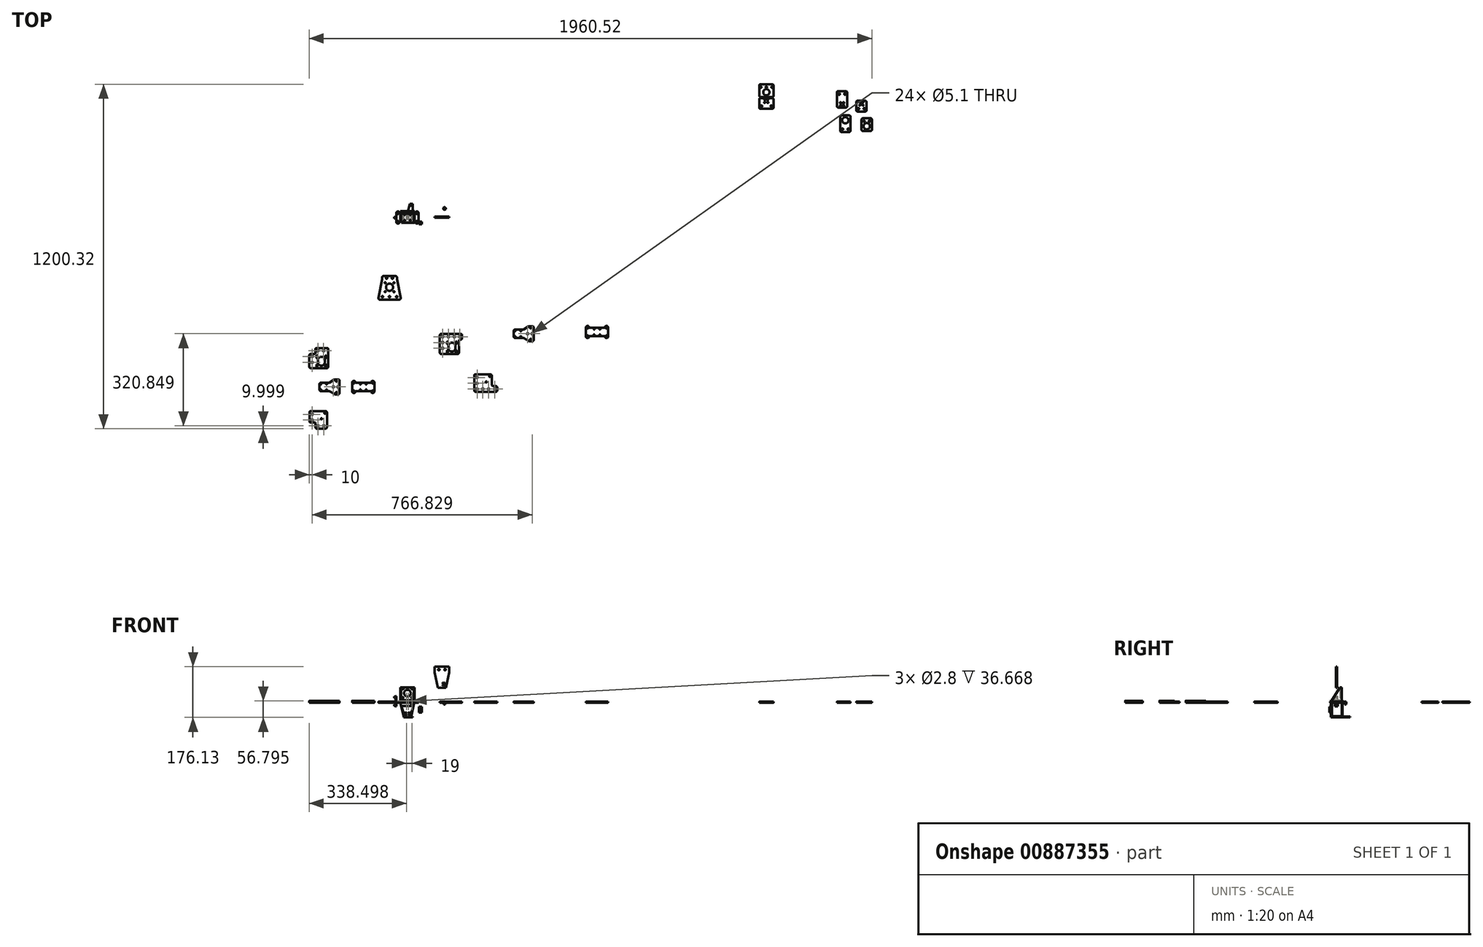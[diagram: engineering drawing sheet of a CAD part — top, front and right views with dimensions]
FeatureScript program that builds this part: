
annotation { "Feature Type Name" : "Feature", "Feature Type Description" : "" }
export const myFeature = defineFeature(function(context is Context, id is Id, definition is map)
    precondition{}
    {
        {
            var Q0;
            Q0=qCreatedBy(makeId("Top.planeOp"),FACE);
            var sketch = newSketch(context, id + "F0", { "sketchPlane" : qUnion([Q0])});
            skCircle(sketch, "E0", {"center": v(-667.66, -487.54) * mm, "radius": 2.55 * mm});
            skCircle(sketch, "E1", {"center": v(-667.66, -507.54) * mm, "radius": 2.55 * mm});
            skLineSegment(sketch, "E2.top", {"start": v(-677.66, -483.54) * mm, "end": v(-677.66, -522.54) * mm});
            skLineSegment(sketch, "E2.left", {"start": v(-620.16, -457.54) * mm, "end": v(-651.66, -457.54) * mm});
            skLineSegment(sketch, "E2.right", {"start": v(-620.16, -527.54) * mm, "end": v(-672.66, -527.54) * mm});
            skLineSegment(sketch, "E3.top", {"start": v(-656.66, -462.54) * mm, "end": v(-656.66, -478.54) * mm});
            skLineSegment(sketch, "E3.right", {"start": v(-672.66, -478.54) * mm, "end": v(-656.66, -478.54) * mm});
            skLineSegment(sketch, "E4", {"start": v(-620.16, -491.36) * mm, "end": v(-620.16, -485.36) * mm});
            skLineSegment(sketch, "E5", {"start": v(-651.16, -491.36) * mm, "end": v(-651.16, -485.36) * mm});
            skLineSegment(sketch, "E6", {"start": v(-620.16, -522.36) * mm, "end": v(-620.16, -516.36) * mm});
            skLineSegment(sketch, "E7", {"start": v(-623.41, -500.36) * mm, "end": v(-623.41, -506.86) * mm});
            skLineSegment(sketch, "E8", {"start": v(-647.91, -500.36) * mm, "end": v(-647.91, -506.86) * mm});
            skArc(sketch, "E9", {"start": v(-623.41, -500.36) * mm, "mid": v(-635.66, -488.1) * mm, "end": v(-647.91, -500.36) * mm});
            skArc(sketch, "E10", {"start": v(-647.91, -506.86) * mm, "mid": v(-635.66, -519.1) * mm, "end": v(-623.41, -506.86) * mm});
            skLineSegment(sketch, "E11", {"start": v(-621.75, -516.3) * mm, "end": v(-621.75, -522.32) * mm});
            skLineSegment(sketch, "E12", {"start": v(-618.57, -516.3) * mm, "end": v(-618.57, -522.32) * mm});
            skLineSegment(sketch, "E13", {"start": v(-649.58, -516.27) * mm, "end": v(-649.57, -522.32) * mm});
            skLineSegment(sketch, "E14", {"start": v(-652.75, -516.3) * mm, "end": v(-652.75, -522.35) * mm});
            skLineSegment(sketch, "E15", {"start": v(-651.16, -516.36) * mm, "end": v(-651.16, -522.36) * mm});
            skLineSegment(sketch, "E16", {"start": v(-652.75, -485.36) * mm, "end": v(-652.75, -491.37) * mm});
            skLineSegment(sketch, "E17", {"start": v(-649.57, -485.36) * mm, "end": v(-649.57, -491.37) * mm});
            skLineSegment(sketch, "E18", {"start": v(-621.75, -485.35) * mm, "end": v(-621.75, -491.35) * mm});
            skLineSegment(sketch, "E19", {"start": v(-618.57, -485.35) * mm, "end": v(-618.57, -491.35) * mm});
            skArc(sketch, "E20", {"start": v(-618.57, -485.35) * mm, "mid": v(-620.16, -483.76) * mm, "end": v(-621.75, -485.35) * mm});
            skArc(sketch, "E21", {"start": v(-621.75, -491.35) * mm, "mid": v(-620.16, -492.94) * mm, "end": v(-618.57, -491.35) * mm});
            skArc(sketch, "E22", {"start": v(-649.57, -485.36) * mm, "mid": v(-651.16, -483.77) * mm, "end": v(-652.75, -485.36) * mm});
            skArc(sketch, "E23", {"start": v(-652.75, -491.37) * mm, "mid": v(-651.16, -492.96) * mm, "end": v(-649.57, -491.37) * mm});
            skArc(sketch, "E24", {"start": v(-649.58, -516.27) * mm, "mid": v(-651.18, -514.72) * mm, "end": v(-652.75, -516.3) * mm});
            skArc(sketch, "E25", {"start": v(-652.75, -522.35) * mm, "mid": v(-651.14, -523.94) * mm, "end": v(-649.57, -522.32) * mm});
            skArc(sketch, "E26", {"start": v(-621.75, -522.32) * mm, "mid": v(-620.16, -523.9) * mm, "end": v(-618.57, -522.32) * mm});
            skArc(sketch, "E27", {"start": v(-618.57, -516.3) * mm, "mid": v(-620.16, -514.72) * mm, "end": v(-621.75, -516.3) * mm});
            skArc(sketch, "E28.filletArc", {"start": v(-651.66, -457.54) * mm, "mid": v(-655.2, -459) * mm, "end": v(-656.66, -462.54) * mm});
            skArc(sketch, "E29.filletArc", {"start": v(-672.66, -478.54) * mm, "mid": v(-676.2, -480) * mm, "end": v(-677.66, -483.54) * mm});
            skArc(sketch, "E30.filletArc", {"start": v(-677.66, -522.54) * mm, "mid": v(-676.2, -526.07) * mm, "end": v(-672.66, -527.54) * mm});
            skCircle(sketch, "E31", {"center": v(-635.1, -704.3) * mm, "radius": 2.05 * mm});
            skLineSegment(sketch, "E32.top", {"start": v(-651.1, -738.6) * mm, "end": v(-624.1, -738.6) * mm});
            skLineSegment(sketch, "E32.left", {"start": v(-677.1, -682.25) * mm, "end": v(-677.1, -712.6) * mm});
            skLineSegment(sketch, "E33.top", {"start": v(-672.1, -717.6) * mm, "end": v(-656.1, -717.6) * mm});
            skLineSegment(sketch, "E33.right", {"start": v(-656.1, -733.6) * mm, "end": v(-656.1, -717.6) * mm});
            skLineSegment(sketch, "E34", {"start": v(-672.1, -677.25) * mm, "end": v(-624.1, -677.25) * mm});
            skArc(sketch, "E35.filletArc", {"start": v(-672.1, -677.25) * mm, "mid": v(-675.64, -678.71) * mm, "end": v(-677.1, -682.25) * mm});
            skArc(sketch, "E36.filletArc", {"start": v(-656.1, -733.6) * mm, "mid": v(-654.64, -737.14) * mm, "end": v(-651.1, -738.6) * mm});
            skArc(sketch, "E37.filletArc", {"start": v(-677.1, -712.6) * mm, "mid": v(-675.64, -716.14) * mm, "end": v(-672.1, -717.6) * mm});
            skCircle(sketch, "E38", {"center": v(-623.1, -684.37) * mm, "radius": 2.05 * mm});
            skCircle(sketch, "E39", {"center": v(-499.55, -583.25) * mm, "radius": 1.59 * mm});
            skCircle(sketch, "E40", {"center": v(-479.55, -583.25) * mm, "radius": 1.59 * mm});
            skCircle(sketch, "E41", {"center": v(-499.55, -603.25) * mm, "radius": 1.59 * mm});
            skCircle(sketch, "E42", {"center": v(-479.55, -603.25) * mm, "radius": 1.59 * mm});
            skLineSegment(sketch, "E43", {"start": v(-515.07, -607.95) * mm, "end": v(-515.07, -608) * mm});
            skCircle(sketch, "E44", {"center": v(-457.05, -579.25) * mm, "radius": 2.05 * mm});
            skCircle(sketch, "E45", {"center": v(-457.05, -607.25) * mm, "radius": 2.05 * mm});
            skCircle(sketch, "E46", {"center": v(-522.05, -607.25) * mm, "radius": 2.05 * mm});
            skCircle(sketch, "E47", {"center": v(-522.05, -579.25) * mm, "radius": 2.05 * mm});
            skLineSegment(sketch, "E48.right", {"start": v(-517, -577.2) * mm, "end": v(-517, -609.3) * mm});
            skLineSegment(sketch, "E49.left", {"start": v(-462.1, -577.2) * mm, "end": v(-462.1, -609.3) * mm});
            skLineSegment(sketch, "E50.bottom", {"start": v(-504.14, -578.67) * mm, "end": v(-474.96, -578.67) * mm});
            skLineSegment(sketch, "E50.top", {"start": v(-504.14, -607.84) * mm, "end": v(-474.96, -607.84) * mm});
            skPoint(sketch, "E51.visualSharp", {"position": v(-462.1, -574.2) * mm});
            skPoint(sketch, "E52.visualSharp", {"position": v(-452, -574.2) * mm});
            skPoint(sketch, "E53.visualSharp", {"position": v(-452, -612.3) * mm});
            skPoint(sketch, "E54.visualSharp", {"position": v(-462.1, -612.3) * mm});
            skLineSegment(sketch, "E55", {"start": v(-504.14, -607.84) * mm, "end": v(-517.38, -607.84) * mm});
            skLineSegment(sketch, "E56", {"start": v(-504.14, -578.67) * mm, "end": v(-517, -578.67) * mm});
            skLineSegment(sketch, "E57", {"start": v(-474.96, -578.67) * mm, "end": v(-461.72, -578.67) * mm});
            skLineSegment(sketch, "E58", {"start": v(-474.96, -607.84) * mm, "end": v(-462.1, -607.84) * mm});
            skCircle(sketch, "E59", {"center": v(-593.62, -593.18) * mm, "radius": 2.55 * mm});
            skCircle(sketch, "E60", {"center": v(-577.62, -593.18) * mm, "radius": 2.55 * mm});
            skCircle(sketch, "E61", {"center": v(-637.35, -583.18) * mm, "radius": 1.59 * mm});
            skCircle(sketch, "E62", {"center": v(-617.35, -583.18) * mm, "radius": 1.59 * mm});
            skCircle(sketch, "E63", {"center": v(-637.35, -603.18) * mm, "radius": 1.59 * mm});
            skCircle(sketch, "E64", {"center": v(-617.35, -603.18) * mm, "radius": 1.59 * mm});
            skCircle(sketch, "E65", {"center": v(-583.36, -573.09) * mm, "radius": 2.05 * mm});
            skCircle(sketch, "E66", {"center": v(-583.36, -613.09) * mm, "radius": 2.05 * mm});
            skLineSegment(sketch, "E67", {"start": v(-572.07, -612.16) * mm, "end": v(-572.07, -573.88) * mm});
            skLineSegment(sketch, "E68", {"start": v(-637.35, -578.6) * mm, "end": v(-607.62, -578.6) * mm});
            skLineSegment(sketch, "E69", {"start": v(-637.17, -607.77) * mm, "end": v(-607.63, -607.78) * mm});
            skLineSegment(sketch, "E70", {"start": v(-642.17, -602.81) * mm, "end": v(-642.35, -583.64) * mm});
            skPoint(sketch, "E71.visualSharp", {"position": v(-572.07, -617.16) * mm});
            skPoint(sketch, "E72.visualSharp", {"position": v(-572.07, -568.86) * mm});
            skPoint(sketch, "E73.visualSharp", {"position": v(-642.12, -607.76) * mm});
            skArc(sketch, "E73.filletArc", {"start": v(-642.17, -602.81) * mm, "mid": v(-640.69, -606.32) * mm, "end": v(-637.17, -607.77) * mm});
            skPoint(sketch, "E74.visualSharp", {"position": v(-642.4, -578.59) * mm});
            skArc(sketch, "E74.filletArc", {"start": v(-637.35, -578.6) * mm, "mid": v(-640.9, -580.07) * mm, "end": v(-642.35, -583.64) * mm});
            skLineSegment(sketch, "E75.bottom", {"start": v(-624.1, -677.25) * mm, "end": v(-621.05, -677.25) * mm});
            skLineSegment(sketch, "E75.top", {"start": v(-624.1, -738.6) * mm, "end": v(-621.05, -738.6) * mm});
            skLineSegment(sketch, "E75.right", {"start": v(-616.05, -682.25) * mm, "end": v(-616.05, -733.6) * mm});
            skPoint(sketch, "E76.visualSharp", {"position": v(-616.05, -677.25) * mm});
            skArc(sketch, "E76.filletArc", {"start": v(-616.05, -682.25) * mm, "mid": v(-617.52, -678.71) * mm, "end": v(-621.05, -677.25) * mm});
            skPoint(sketch, "E77.visualSharp", {"position": v(-616.05, -738.6) * mm});
            skArc(sketch, "E77.filletArc", {"start": v(-621.05, -738.6) * mm, "mid": v(-617.52, -737.14) * mm, "end": v(-616.05, -733.6) * mm});
            skLineSegment(sketch, "E78.bottom", {"start": v(-522, -572.2) * mm, "end": v(-523.1, -572.2) * mm});
            skLineSegment(sketch, "E78.top", {"start": v(-522, -614.3) * mm, "end": v(-523.1, -614.3) * mm});
            skLineSegment(sketch, "E78.right", {"start": v(-528.1, -577.2) * mm, "end": v(-528.1, -609.3) * mm});
            skLineSegment(sketch, "E79.bottom", {"start": v(-457.1, -614.3) * mm, "end": v(-456, -614.3) * mm});
            skLineSegment(sketch, "E79.top", {"start": v(-457.1, -572.2) * mm, "end": v(-456, -572.2) * mm});
            skLineSegment(sketch, "E79.left", {"start": v(-462.1, -609.3) * mm, "end": v(-462.1, -577.2) * mm});
            skLineSegment(sketch, "E79.right", {"start": v(-451, -609.3) * mm, "end": v(-451, -577.2) * mm});
            skPoint(sketch, "E80.visualSharp", {"position": v(-528.1, -572.2) * mm});
            skArc(sketch, "E80.filletArc", {"start": v(-523.1, -572.2) * mm, "mid": v(-526.63, -573.67) * mm, "end": v(-528.1, -577.2) * mm});
            skPoint(sketch, "E81.visualSharp", {"position": v(-517, -572.2) * mm});
            skArc(sketch, "E81.filletArc", {"start": v(-517, -577.2) * mm, "mid": v(-518.46, -573.67) * mm, "end": v(-522, -572.2) * mm});
            skPoint(sketch, "E82.visualSharp", {"position": v(-528.1, -614.3) * mm});
            skArc(sketch, "E82.filletArc", {"start": v(-528.1, -609.3) * mm, "mid": v(-526.63, -612.84) * mm, "end": v(-523.1, -614.3) * mm});
            skPoint(sketch, "E83.visualSharp", {"position": v(-517, -614.3) * mm});
            skArc(sketch, "E83.filletArc", {"start": v(-522, -614.3) * mm, "mid": v(-518.46, -612.84) * mm, "end": v(-517, -609.3) * mm});
            skPoint(sketch, "E84.visualSharp", {"position": v(-462.1, -572.2) * mm});
            skArc(sketch, "E84.filletArc", {"start": v(-457.1, -572.2) * mm, "mid": v(-460.63, -573.67) * mm, "end": v(-462.1, -577.2) * mm});
            skPoint(sketch, "E85.visualSharp", {"position": v(-451, -572.2) * mm});
            skArc(sketch, "E85.filletArc", {"start": v(-451, -577.2) * mm, "mid": v(-452.46, -573.67) * mm, "end": v(-456, -572.2) * mm});
            skPoint(sketch, "E86.visualSharp", {"position": v(-451, -614.3) * mm});
            skArc(sketch, "E86.filletArc", {"start": v(-456, -614.3) * mm, "mid": v(-452.46, -612.84) * mm, "end": v(-451, -609.3) * mm});
            skPoint(sketch, "E87.visualSharp", {"position": v(-462.1, -614.3) * mm});
            skArc(sketch, "E87.filletArc", {"start": v(-462.1, -609.3) * mm, "mid": v(-460.63, -612.84) * mm, "end": v(-457.1, -614.3) * mm});
            skLineSegment(sketch, "E88.bottom", {"start": v(-587.09, -566.93) * mm, "end": v(-577.07, -566.93) * mm});
            skLineSegment(sketch, "E88.right", {"start": v(-572.07, -571.93) * mm, "end": v(-572.07, -573.88) * mm});
            skLineSegment(sketch, "E89.bottom", {"start": v(-586.95, -619.16) * mm, "end": v(-577.07, -619.16) * mm});
            skLineSegment(sketch, "E89.right", {"start": v(-572.07, -614.16) * mm, "end": v(-572.07, -612.16) * mm});
            skLineSegment(sketch, "E90", {"start": v(-607.62, -578.6) * mm, "end": v(-589.7, -567.66) * mm});
            skLineSegment(sketch, "E91", {"start": v(-607.63, -607.78) * mm, "end": v(-589.48, -618.47) * mm});
            skPoint(sketch, "E92.visualSharp", {"position": v(-588.5, -566.93) * mm});
            skArc(sketch, "E92.filletArc", {"start": v(-587.09, -566.93) * mm, "mid": v(-588.44, -567.11) * mm, "end": v(-589.7, -567.66) * mm});
            skPoint(sketch, "E93.visualSharp", {"position": v(-572.07, -566.93) * mm});
            skArc(sketch, "E93.filletArc", {"start": v(-572.07, -571.93) * mm, "mid": v(-573.54, -568.4) * mm, "end": v(-577.07, -566.93) * mm});
            skPoint(sketch, "E94.visualSharp", {"position": v(-572.07, -619.16) * mm});
            skArc(sketch, "E94.filletArc", {"start": v(-577.07, -619.16) * mm, "mid": v(-573.54, -617.7) * mm, "end": v(-572.07, -614.16) * mm});
            skPoint(sketch, "E95.visualSharp", {"position": v(-588.3, -619.16) * mm});
            skArc(sketch, "E95.filletArc", {"start": v(-589.48, -618.47) * mm, "mid": v(-588.26, -618.98) * mm, "end": v(-586.95, -619.16) * mm});
            skCircle(sketch, "E96", {"center": v(-647.66, -467.54) * mm, "radius": 2.55 * mm});
            skCircle(sketch, "E97", {"center": v(-627.66, -467.54) * mm, "radius": 2.55 * mm});
            skLineSegment(sketch, "E98.bottom", {"start": v(-620.16, -457.54) * mm, "end": v(-616.11, -457.54) * mm});
            skLineSegment(sketch, "E98.top", {"start": v(-620.16, -527.54) * mm, "end": v(-616.11, -527.54) * mm});
            skLineSegment(sketch, "E98.right", {"start": v(-611.11, -462.54) * mm, "end": v(-611.11, -522.54) * mm});
            skPoint(sketch, "E99.visualSharp", {"position": v(-611.11, -457.54) * mm});
            skArc(sketch, "E99.filletArc", {"start": v(-611.11, -462.54) * mm, "mid": v(-612.57, -459) * mm, "end": v(-616.11, -457.54) * mm});
            skPoint(sketch, "E100.visualSharp", {"position": v(-611.11, -527.54) * mm});
            skArc(sketch, "E100.filletArc", {"start": v(-616.11, -527.54) * mm, "mid": v(-612.57, -526.07) * mm, "end": v(-611.11, -522.54) * mm});
            skCircle(sketch, "E101", {"center": v(-667.1, -708.6) * mm, "radius": 2.55 * mm});
            skCircle(sketch, "E102", {"center": v(-647.1, -728.6) * mm, "radius": 2.55 * mm});
            skCircle(sketch, "E103", {"center": v(-627.1, -728.6) * mm, "radius": 2.55 * mm});
            skCircle(sketch, "E104", {"center": v(-667.1, -688.6) * mm, "radius": 2.55 * mm});
            skLineSegment(sketch, "E105.top", {"start": v(-677.1, -738.6) * mm, "end": v(-651.1, -738.6) * mm, "construction": true});
            skLineSegment(sketch, "E105.left", {"start": v(-677.1, -712.6) * mm, "end": v(-677.1, -738.6) * mm, "construction": true});
            skLineSegment(sketch, "E106.top", {"start": v(-677.66, -457.54) * mm, "end": v(-651.66, -457.54) * mm, "construction": true});
            skLineSegment(sketch, "E106.left", {"start": v(-677.66, -483.54) * mm, "end": v(-677.66, -457.54) * mm, "construction": true});
            skSolve(sketch);
        }
        {
            var Q0;
            {var subQ1=sQuery(id+"F0.wireOp",EDGE,"E75.bottom");Q0=makeQuery(id+"F0.imprint","IMPRINT",FACE,{"disambiguationData":[TD([[makeQuery(id+"F0.imprint","IMPRINT",EDGE,{"derivedFrom":subQ1}),-1.0]])]});}
            var Q1;
            Q1=makeQuery(id+"F0.imprint","IMPRINT",FACE,{"disambiguationData":[TD([[makeQuery(id+"F0.imprint","IMPRINT",EDGE,{"derivedFrom":sQuery(id+"F0.wireOp",EDGE,"E44")}),-1.0]])]});
            var Q2;
            Q2=makeQuery(id+"F0.imprint","IMPRINT",FACE,{"disambiguationData":[TD([[makeQuery(id+"F0.imprint","IMPRINT",EDGE,{"derivedFrom":sQuery(id+"F0.wireOp",EDGE,"E46")}),-1.0]])]});
            var Q3;
            {var subQ10=sQuery(id+"F0.wireOp",EDGE,"E12");Q3=makeQuery(id+"F0.imprint","IMPRINT",FACE,{"disambiguationData":[TD([[makeQuery(id+"F0.imprint","IMPRINT",EDGE,{"derivedFrom":subQ10}),1.0]])]});}
            var Q4;
            Q4=makeQuery(id+"F0.imprint","IMPRINT",FACE,{"disambiguationData":[TD([[makeQuery(id+"F0.imprint","IMPRINT",EDGE,{"derivedFrom":sQuery(id+"F0.wireOp",EDGE,"b826868f-84ae-415a-b8de-01fa488b9e32")}),-1.0]])]});
            var Q5;
            Q5=makeQuery(id+"F0.imprint","IMPRINT",FACE,{"disambiguationData":[TD([[makeQuery(id+"F0.imprint","IMPRINT",EDGE,{"derivedFrom":sQuery(id+"F0.wireOp",EDGE,"E39")}),-1.0]])]});
            var Q6;
            Q6=makeQuery(id+"F0.imprint","IMPRINT",FACE,{"disambiguationData":[TD([[makeQuery(id+"F0.imprint","IMPRINT",EDGE,{"derivedFrom":sQuery(id+"F0.wireOp",EDGE,"E31")}),-1.0]])]});
            var Q7;
            Q7=makeQuery(id+"F0.imprint","IMPRINT",FACE,{"disambiguationData":[TD([[makeQuery(id+"F0.imprint","IMPRINT",EDGE,{"derivedFrom":sQuery(id+"F0.wireOp",EDGE,"1adb1561-edb4-4775-b7b4-249f5b53a184")}),-1.0]])]});
            var Q8;
            Q8=makeQuery(id+"F0.imprint","IMPRINT",FACE,{"disambiguationData":[TD([[makeQuery(id+"F0.imprint","IMPRINT",EDGE,{"derivedFrom":sQuery(id+"F0.wireOp",EDGE,"be8f3962-e8e7-4b8b-97a9-2f4c6b4b087e")}),-1.0]])]});
            var Q9;
            Q9=makeQuery(id+"F0.imprint","IMPRINT",FACE,{"disambiguationData":[TD([[makeQuery(id+"F0.imprint","IMPRINT",EDGE,{"derivedFrom":sQuery(id+"F0.wireOp",EDGE,"084fcb39-8721-4a62-9619-5143ccd3a1a7")}),-1.0]])]});
            var Q10;
            Q10=makeQuery(id+"F0.imprint","IMPRINT",FACE,{"disambiguationData":[TD([[makeQuery(id+"F0.imprint","IMPRINT",EDGE,{"derivedFrom":sQuery(id+"F0.wireOp",EDGE,"E59")}),-1.0]])]});
            var Q11;
            Q11=makeQuery(id+"F0.imprint","IMPRINT",FACE,{"disambiguationData":[TD([[makeQuery(id+"F0.imprint","IMPRINT",EDGE,{"derivedFrom":sQuery(id+"F0.wireOp",EDGE,"9dac7aaf-eed2-4e08-89de-ef89cb368206")}),-1.0]])]});
            var Q12;
            Q12=makeQuery(id+"F0.imprint","IMPRINT",FACE,{"disambiguationData":[TD([[makeQuery(id+"F0.imprint","IMPRINT",EDGE,{"derivedFrom":sQuery(id+"F0.wireOp",EDGE,"E0")}),-1.0]])]});
            extrude(context, id + "F1", {"entities" : qUnion([Q0, Q1, Q2, Q3, Q4, Q5, Q6, Q7, Q8, Q9, Q10, Q11, Q12]), "depth" : 6.35 * mm, "offsetDistance" : 25 * mm});
        }
        {
            var Q0;
            Q0=qCreatedBy(makeId("Top.planeOp"),FACE);
            var sketch = newSketch(context, id + "F2", { "sketchPlane" : qUnion([Q0])});
            skCircle(sketch, "E107", {"center": v(-212.74, -438.4) * mm, "radius": 2.55 * mm});
            skCircle(sketch, "E108", {"center": v(-212.74, -458.4) * mm, "radius": 2.55 * mm});
            skLineSegment(sketch, "E109.top", {"start": v(-222.74, -434.4) * mm, "end": v(-222.74, -473.4) * mm});
            skLineSegment(sketch, "E109.left", {"start": v(-125.8, -408.4) * mm, "end": v(-196.74, -408.4) * mm});
            skLineSegment(sketch, "E109.right", {"start": v(-165.24, -478.4) * mm, "end": v(-217.74, -478.4) * mm});
            skLineSegment(sketch, "E110.top", {"start": v(-201.74, -413.4) * mm, "end": v(-201.74, -429.4) * mm});
            skLineSegment(sketch, "E110.right", {"start": v(-217.74, -429.4) * mm, "end": v(-201.74, -429.4) * mm});
            skLineSegment(sketch, "E111", {"start": v(-165.24, -442.21) * mm, "end": v(-165.24, -436.21) * mm});
            skLineSegment(sketch, "E112", {"start": v(-196.24, -442.21) * mm, "end": v(-196.24, -436.21) * mm});
            skLineSegment(sketch, "E113", {"start": v(-165.24, -473.21) * mm, "end": v(-165.24, -467.21) * mm});
            skLineSegment(sketch, "E114", {"start": v(-168.5, -451.22) * mm, "end": v(-168.5, -457.72) * mm});
            skLineSegment(sketch, "E115", {"start": v(-193, -451.22) * mm, "end": v(-193, -457.72) * mm});
            skArc(sketch, "E116", {"start": v(-168.5, -451.22) * mm, "mid": v(-180.74, -438.97) * mm, "end": v(-193, -451.22) * mm});
            skArc(sketch, "E117", {"start": v(-193, -457.72) * mm, "mid": v(-180.74, -469.97) * mm, "end": v(-168.5, -457.72) * mm});
            skLineSegment(sketch, "E118", {"start": v(-166.83, -467.16) * mm, "end": v(-166.83, -473.17) * mm});
            skLineSegment(sketch, "E119", {"start": v(-163.66, -467.16) * mm, "end": v(-163.66, -473.17) * mm});
            skLineSegment(sketch, "E120", {"start": v(-194.66, -467.13) * mm, "end": v(-194.66, -473.17) * mm});
            skLineSegment(sketch, "E121", {"start": v(-197.83, -467.17) * mm, "end": v(-197.83, -473.2) * mm});
            skLineSegment(sketch, "E122", {"start": v(-196.24, -467.21) * mm, "end": v(-196.24, -473.21) * mm});
            skLineSegment(sketch, "E123", {"start": v(-197.83, -436.21) * mm, "end": v(-197.83, -442.23) * mm});
            skLineSegment(sketch, "E124", {"start": v(-194.66, -436.21) * mm, "end": v(-194.66, -442.23) * mm});
            skLineSegment(sketch, "E125", {"start": v(-166.83, -436.2) * mm, "end": v(-166.83, -442.2) * mm});
            skLineSegment(sketch, "E126", {"start": v(-163.66, -436.2) * mm, "end": v(-163.66, -442.2) * mm});
            skArc(sketch, "E127", {"start": v(-163.66, -436.2) * mm, "mid": v(-165.24, -434.62) * mm, "end": v(-166.83, -436.2) * mm});
            skArc(sketch, "E128", {"start": v(-166.83, -442.2) * mm, "mid": v(-165.24, -443.8) * mm, "end": v(-163.66, -442.2) * mm});
            skArc(sketch, "E129", {"start": v(-194.66, -436.21) * mm, "mid": v(-196.24, -434.62) * mm, "end": v(-197.83, -436.21) * mm});
            skArc(sketch, "E130", {"start": v(-197.83, -442.23) * mm, "mid": v(-196.24, -443.82) * mm, "end": v(-194.66, -442.23) * mm});
            skArc(sketch, "E131", {"start": v(-194.66, -467.13) * mm, "mid": v(-196.26, -465.58) * mm, "end": v(-197.83, -467.17) * mm});
            skArc(sketch, "E132", {"start": v(-197.83, -473.2) * mm, "mid": v(-196.23, -474.8) * mm, "end": v(-194.66, -473.17) * mm});
            skArc(sketch, "E133", {"start": v(-166.83, -473.17) * mm, "mid": v(-165.24, -474.76) * mm, "end": v(-163.66, -473.17) * mm});
            skArc(sketch, "E134", {"start": v(-163.66, -467.16) * mm, "mid": v(-165.24, -465.58) * mm, "end": v(-166.83, -467.16) * mm});
            skArc(sketch, "E135.filletArc", {"start": v(-196.74, -408.4) * mm, "mid": v(-200.28, -409.86) * mm, "end": v(-201.74, -413.4) * mm});
            skArc(sketch, "E136.filletArc", {"start": v(-217.74, -429.4) * mm, "mid": v(-221.28, -430.86) * mm, "end": v(-222.74, -434.4) * mm});
            skArc(sketch, "E137.filletArc", {"start": v(-222.74, -473.4) * mm, "mid": v(-221.28, -476.93) * mm, "end": v(-217.74, -478.4) * mm});
            skCircle(sketch, "E138", {"center": v(-192.74, -418.4) * mm, "radius": 2.55 * mm});
            skCircle(sketch, "E139", {"center": v(-172.74, -418.4) * mm, "radius": 2.55 * mm});
            skLineSegment(sketch, "E140.bottom", {"start": v(-161.2, -408.4) * mm, "end": v(-150.06, -408.4) * mm});
            skLineSegment(sketch, "E140.top", {"start": v(-165.24, -478.4) * mm, "end": v(-161.2, -478.4) * mm});
            skPoint(sketch, "E141.visualSharp", {"position": v(-156.2, -408.4) * mm});
            skPoint(sketch, "E142.visualSharp", {"position": v(-156.2, -478.4) * mm});
            skArc(sketch, "E142.filletArc", {"start": v(-161.2, -478.4) * mm, "mid": v(-157.66, -476.93) * mm, "end": v(-156.2, -473.4) * mm});
            skLineSegment(sketch, "E143", {"start": v(-196.74, -408.4) * mm, "end": v(-217.74, -408.4) * mm});
            skLineSegment(sketch, "E144", {"start": v(-222.74, -413.4) * mm, "end": v(-222.74, -434.4) * mm});
            skPoint(sketch, "E145.visualSharp", {"position": v(-222.74, -408.4) * mm});
            skArc(sketch, "E145.filletArc", {"start": v(-217.74, -408.4) * mm, "mid": v(-221.28, -409.86) * mm, "end": v(-222.74, -413.4) * mm});
            skCircle(sketch, "E146", {"center": v(-212.74, -418.4) * mm, "radius": 2.55 * mm});
            skCircle(sketch, "E147", {"center": v(-152.74, -418.4) * mm, "radius": 2.55 * mm});
            skLineSegment(sketch, "E148.bottom", {"start": v(-165.19, -408.4) * mm, "end": v(-145.06, -408.4) * mm});
            skLineSegment(sketch, "E148.right", {"start": v(-145.06, -413.4) * mm, "end": v(-145.06, -423.4) * mm});
            skPoint(sketch, "E149.newPointB", {"position": v(-145.06, -408.4) * mm});
            skArc(sketch, "E149.filletArc", {"start": v(-145.06, -413.4) * mm, "mid": v(-146.53, -409.86) * mm, "end": v(-150.06, -408.4) * mm});
            skPoint(sketch, "E150.visualSharp", {"position": v(-145.06, -428.4) * mm});
            skArc(sketch, "E150.filletArc", {"start": v(-150.06, -428.4) * mm, "mid": v(-146.53, -426.93) * mm, "end": v(-145.06, -423.4) * mm});
            skLineSegment(sketch, "E151", {"start": v(-150.06, -428.4) * mm, "end": v(-156.2, -428.4) * mm});
            skLineSegment(sketch, "E152", {"start": v(-156.2, -428.4) * mm, "end": v(-156.2, -473.4) * mm});
            skSolve(sketch);
        }
        {
            var Q0;
            Q0=qCreatedBy(makeId("Top.planeOp"),FACE);
            var sketch = newSketch(context, id + "F3", { "sketchPlane" : qUnion([Q0])});
            skCircle(sketch, "E153", {"center": v(-60.9, -576.03) * mm, "radius": 2.05 * mm});
            skLineSegment(sketch, "E154.top", {"start": v(-76.9, -610.34) * mm, "end": v(-49.9, -610.34) * mm});
            skLineSegment(sketch, "E154.left", {"start": v(-102.9, -553.98) * mm, "end": v(-102.9, -584.34) * mm});
            skLineSegment(sketch, "E155.top", {"start": v(-97.9, -589.34) * mm, "end": v(-81.9, -589.34) * mm});
            skLineSegment(sketch, "E155.right", {"start": v(-81.9, -605.34) * mm, "end": v(-81.9, -589.34) * mm});
            skLineSegment(sketch, "E156", {"start": v(-97.9, -548.98) * mm, "end": v(-49.9, -548.98) * mm});
            skArc(sketch, "E157.filletArc", {"start": v(-97.9, -548.98) * mm, "mid": v(-101.44, -550.45) * mm, "end": v(-102.9, -553.98) * mm});
            skArc(sketch, "E158.filletArc", {"start": v(-81.9, -605.34) * mm, "mid": v(-80.44, -608.87) * mm, "end": v(-76.9, -610.34) * mm});
            skArc(sketch, "E159.filletArc", {"start": v(-102.9, -584.34) * mm, "mid": v(-101.44, -587.87) * mm, "end": v(-97.9, -589.34) * mm});
            skCircle(sketch, "E160", {"center": v(-48.9, -556.1) * mm, "radius": 2.05 * mm});
            skLineSegment(sketch, "E161.bottom", {"start": v(-49.9, -548.98) * mm, "end": v(-46.85, -548.98) * mm});
            skLineSegment(sketch, "E161.top", {"start": v(-49.9, -610.34) * mm, "end": v(-46.85, -610.34) * mm});
            skLineSegment(sketch, "E161.right", {"start": v(-41.85, -553.98) * mm, "end": v(-41.85, -585.34) * mm});
            skPoint(sketch, "E162.visualSharp", {"position": v(-41.85, -548.98) * mm});
            skArc(sketch, "E162.filletArc", {"start": v(-41.85, -553.98) * mm, "mid": v(-43.31, -550.45) * mm, "end": v(-46.85, -548.98) * mm});
            skPoint(sketch, "E163.visualSharp", {"position": v(-41.85, -610.34) * mm});
            skCircle(sketch, "E164", {"center": v(-92.9, -580.34) * mm, "radius": 2.55 * mm});
            skCircle(sketch, "E165", {"center": v(-72.9, -600.34) * mm, "radius": 2.55 * mm});
            skCircle(sketch, "E166", {"center": v(-52.9, -600.34) * mm, "radius": 2.55 * mm});
            skCircle(sketch, "E167", {"center": v(-92.9, -560.34) * mm, "radius": 2.55 * mm});
            skPoint(sketch, "E168.visualSharp", {"position": v(-102.9, -610.34) * mm});
            skLineSegment(sketch, "E169", {"start": v(-102.9, -584.34) * mm, "end": v(-102.9, -605.34) * mm});
            skLineSegment(sketch, "E170", {"start": v(-76.9, -610.34) * mm, "end": v(-97.9, -610.34) * mm});
            skArc(sketch, "E171.filletArc", {"start": v(-102.9, -605.34) * mm, "mid": v(-101.44, -608.87) * mm, "end": v(-97.9, -610.34) * mm});
            skCircle(sketch, "E172", {"center": v(-92.9, -600.34) * mm, "radius": 2.55 * mm});
            skCircle(sketch, "E173", {"center": v(-31.4, -600.34) * mm, "radius": 2.55 * mm});
            skLineSegment(sketch, "E174.bottom", {"start": v(-46.85, -610.34) * mm, "end": v(-27.85, -610.34) * mm});
            skLineSegment(sketch, "E174.top", {"start": v(-36.85, -590.34) * mm, "end": v(-27.85, -590.34) * mm});
            skLineSegment(sketch, "E174.right", {"start": v(-22.85, -605.34) * mm, "end": v(-22.85, -595.34) * mm});
            skArc(sketch, "E175.filletArc", {"start": v(-41.85, -585.34) * mm, "mid": v(-40.39, -588.87) * mm, "end": v(-36.85, -590.34) * mm});
            skPoint(sketch, "E176.visualSharp", {"position": v(-22.85, -590.34) * mm});
            skArc(sketch, "E176.filletArc", {"start": v(-22.85, -595.34) * mm, "mid": v(-24.31, -591.8) * mm, "end": v(-27.85, -590.34) * mm});
            skPoint(sketch, "E177.visualSharp", {"position": v(-22.85, -610.34) * mm});
            skArc(sketch, "E177.filletArc", {"start": v(-27.85, -610.34) * mm, "mid": v(-24.31, -608.87) * mm, "end": v(-22.85, -605.34) * mm});
            skSolve(sketch);
        }
        {
            var Q0;
            Q0=qCreatedBy(makeId("Top.planeOp"),FACE);
            var sketch = newSketch(context, id + "F4", { "sketchPlane" : qUnion([Q0])});
            skCircle(sketch, "E178", {"center": v(83.17, -407.75) * mm, "radius": 2.55 * mm});
            skCircle(sketch, "E179", {"center": v(99.17, -407.75) * mm, "radius": 2.55 * mm});
            skCircle(sketch, "E180", {"center": v(39.44, -397.75) * mm, "radius": 1.59 * mm});
            skCircle(sketch, "E181", {"center": v(59.44, -397.75) * mm, "radius": 1.59 * mm});
            skCircle(sketch, "E182", {"center": v(39.44, -417.75) * mm, "radius": 1.59 * mm});
            skCircle(sketch, "E183", {"center": v(59.44, -417.75) * mm, "radius": 1.59 * mm});
            skCircle(sketch, "E184", {"center": v(93.43, -387.66) * mm, "radius": 2.05 * mm});
            skCircle(sketch, "E185", {"center": v(93.43, -427.66) * mm, "radius": 2.05 * mm});
            skLineSegment(sketch, "E186", {"start": v(104.72, -426.74) * mm, "end": v(104.72, -388.45) * mm});
            skLineSegment(sketch, "E187", {"start": v(39.45, -393.16) * mm, "end": v(69.17, -393.18) * mm});
            skLineSegment(sketch, "E188", {"start": v(39.62, -422.34) * mm, "end": v(69.16, -422.35) * mm});
            skLineSegment(sketch, "E189", {"start": v(34.62, -417.39) * mm, "end": v(34.44, -398.21) * mm});
            skPoint(sketch, "E190.visualSharp", {"position": v(104.72, -431.74) * mm});
            skPoint(sketch, "E191.visualSharp", {"position": v(104.72, -383.43) * mm});
            skPoint(sketch, "E192.visualSharp", {"position": v(34.67, -422.34) * mm});
            skArc(sketch, "E192.filletArc", {"start": v(34.62, -417.39) * mm, "mid": v(36.1, -420.9) * mm, "end": v(39.62, -422.34) * mm});
            skPoint(sketch, "E193.visualSharp", {"position": v(34.4, -393.16) * mm});
            skArc(sketch, "E193.filletArc", {"start": v(39.45, -393.16) * mm, "mid": v(35.9, -394.64) * mm, "end": v(34.44, -398.21) * mm});
            skLineSegment(sketch, "E194.bottom", {"start": v(89.7, -381.5) * mm, "end": v(99.72, -381.5) * mm});
            skLineSegment(sketch, "E194.right", {"start": v(104.72, -386.5) * mm, "end": v(104.72, -388.45) * mm});
            skLineSegment(sketch, "E195.bottom", {"start": v(89.85, -433.73) * mm, "end": v(99.72, -433.73) * mm});
            skLineSegment(sketch, "E195.right", {"start": v(104.72, -428.73) * mm, "end": v(104.72, -426.74) * mm});
            skLineSegment(sketch, "E196", {"start": v(69.17, -393.18) * mm, "end": v(87.1, -382.23) * mm});
            skLineSegment(sketch, "E197", {"start": v(69.16, -422.35) * mm, "end": v(87.3, -433.04) * mm});
            skPoint(sketch, "E198.visualSharp", {"position": v(88.3, -381.5) * mm});
            skArc(sketch, "E198.filletArc", {"start": v(89.7, -381.5) * mm, "mid": v(88.35, -381.69) * mm, "end": v(87.1, -382.23) * mm});
            skPoint(sketch, "E199.visualSharp", {"position": v(104.72, -381.5) * mm});
            skArc(sketch, "E199.filletArc", {"start": v(104.72, -386.5) * mm, "mid": v(103.25, -382.96) * mm, "end": v(99.72, -381.5) * mm});
            skPoint(sketch, "E200.visualSharp", {"position": v(104.72, -433.73) * mm});
            skArc(sketch, "E200.filletArc", {"start": v(99.72, -433.73) * mm, "mid": v(103.25, -432.27) * mm, "end": v(104.72, -428.73) * mm});
            skPoint(sketch, "E201.visualSharp", {"position": v(88.48, -433.73) * mm});
            skArc(sketch, "E201.filletArc", {"start": v(87.3, -433.04) * mm, "mid": v(88.53, -433.55) * mm, "end": v(89.85, -433.73) * mm});
            skSolve(sketch);
        }
        {
            var Q0;
            Q0=qCreatedBy(makeId("Top.planeOp"),FACE);
            var sketch = newSketch(context, id + "F5", { "sketchPlane" : qUnion([Q0])});
            skCircle(sketch, "E202", {"center": v(315, -391.87) * mm, "radius": 1.59 * mm});
            skCircle(sketch, "E203", {"center": v(335, -391.87) * mm, "radius": 1.59 * mm});
            skCircle(sketch, "E204", {"center": v(315, -411.87) * mm, "radius": 1.59 * mm});
            skCircle(sketch, "E205", {"center": v(335, -411.87) * mm, "radius": 1.59 * mm});
            skLineSegment(sketch, "E206", {"start": v(299.49, -416.57) * mm, "end": v(299.49, -416.62) * mm});
            skCircle(sketch, "E207", {"center": v(357.5, -387.87) * mm, "radius": 2.05 * mm});
            skCircle(sketch, "E208", {"center": v(357.5, -415.87) * mm, "radius": 2.05 * mm});
            skCircle(sketch, "E209", {"center": v(292.5, -415.87) * mm, "radius": 2.05 * mm});
            skCircle(sketch, "E210", {"center": v(292.5, -387.87) * mm, "radius": 2.05 * mm});
            skLineSegment(sketch, "E211.right", {"start": v(297.55, -385.82) * mm, "end": v(297.55, -417.92) * mm});
            skLineSegment(sketch, "E212.left", {"start": v(352.45, -385.82) * mm, "end": v(352.45, -417.92) * mm});
            skLineSegment(sketch, "E213.bottom", {"start": v(310.42, -387.29) * mm, "end": v(339.6, -387.29) * mm});
            skLineSegment(sketch, "E213.top", {"start": v(310.42, -416.46) * mm, "end": v(339.6, -416.46) * mm});
            skPoint(sketch, "E214.visualSharp", {"position": v(352.45, -382.82) * mm});
            skPoint(sketch, "E215.visualSharp", {"position": v(362.55, -382.82) * mm});
            skPoint(sketch, "E216.visualSharp", {"position": v(362.55, -420.92) * mm});
            skPoint(sketch, "E217.visualSharp", {"position": v(352.45, -420.92) * mm});
            skLineSegment(sketch, "E218", {"start": v(310.42, -416.46) * mm, "end": v(297.17, -416.46) * mm});
            skLineSegment(sketch, "E219", {"start": v(310.42, -387.29) * mm, "end": v(297.55, -387.29) * mm});
            skLineSegment(sketch, "E220", {"start": v(339.6, -387.29) * mm, "end": v(352.84, -387.29) * mm});
            skLineSegment(sketch, "E221", {"start": v(339.6, -416.46) * mm, "end": v(352.45, -416.46) * mm});
            skLineSegment(sketch, "E222.bottom", {"start": v(292.55, -380.82) * mm, "end": v(291.45, -380.82) * mm});
            skLineSegment(sketch, "E222.top", {"start": v(292.55, -422.92) * mm, "end": v(291.45, -422.92) * mm});
            skLineSegment(sketch, "E222.right", {"start": v(286.45, -385.82) * mm, "end": v(286.45, -417.92) * mm});
            skLineSegment(sketch, "E223.bottom", {"start": v(357.45, -422.92) * mm, "end": v(358.55, -422.92) * mm});
            skLineSegment(sketch, "E223.top", {"start": v(357.45, -380.82) * mm, "end": v(358.55, -380.82) * mm});
            skLineSegment(sketch, "E223.left", {"start": v(352.45, -417.92) * mm, "end": v(352.45, -385.82) * mm});
            skLineSegment(sketch, "E223.right", {"start": v(363.55, -417.92) * mm, "end": v(363.55, -385.82) * mm});
            skPoint(sketch, "E224.visualSharp", {"position": v(286.45, -380.82) * mm});
            skArc(sketch, "E224.filletArc", {"start": v(291.45, -380.82) * mm, "mid": v(287.92, -382.29) * mm, "end": v(286.45, -385.82) * mm});
            skPoint(sketch, "E225.visualSharp", {"position": v(297.55, -380.82) * mm});
            skArc(sketch, "E225.filletArc", {"start": v(297.55, -385.82) * mm, "mid": v(296.1, -382.29) * mm, "end": v(292.55, -380.82) * mm});
            skPoint(sketch, "E226.visualSharp", {"position": v(286.45, -422.92) * mm});
            skArc(sketch, "E226.filletArc", {"start": v(286.45, -417.92) * mm, "mid": v(287.92, -421.46) * mm, "end": v(291.45, -422.92) * mm});
            skPoint(sketch, "E227.visualSharp", {"position": v(297.55, -422.92) * mm});
            skArc(sketch, "E227.filletArc", {"start": v(292.55, -422.92) * mm, "mid": v(296.1, -421.46) * mm, "end": v(297.55, -417.92) * mm});
            skPoint(sketch, "E228.visualSharp", {"position": v(352.45, -380.82) * mm});
            skArc(sketch, "E228.filletArc", {"start": v(357.45, -380.82) * mm, "mid": v(353.92, -382.29) * mm, "end": v(352.45, -385.82) * mm});
            skPoint(sketch, "E229.visualSharp", {"position": v(363.55, -380.82) * mm});
            skArc(sketch, "E229.filletArc", {"start": v(363.55, -385.82) * mm, "mid": v(362.1, -382.29) * mm, "end": v(358.55, -380.82) * mm});
            skPoint(sketch, "E230.visualSharp", {"position": v(363.55, -422.92) * mm});
            skArc(sketch, "E230.filletArc", {"start": v(358.55, -422.92) * mm, "mid": v(362.1, -421.46) * mm, "end": v(363.55, -417.92) * mm});
            skPoint(sketch, "E231.visualSharp", {"position": v(352.45, -422.92) * mm});
            skArc(sketch, "E231.filletArc", {"start": v(352.45, -417.92) * mm, "mid": v(353.92, -421.46) * mm, "end": v(357.45, -422.92) * mm});
            skSolve(sketch);
        }
        {
            var Q0;
            Q0=makeQuery(id+"F2.imprint","IMPRINT",FACE,{"disambiguationData":[TD([[makeQuery(id+"F2.imprint","IMPRINT",EDGE,{"derivedFrom":sQuery(id+"F2.wireOp",EDGE,"E107")}),-1.0]])]});
            var Q1;
            Q1=makeQuery(id+"F3.imprint","IMPRINT",FACE,{"disambiguationData":[TD([[makeQuery(id+"F3.imprint","IMPRINT",EDGE,{"derivedFrom":sQuery(id+"F3.wireOp",EDGE,"E153")}),-1.0]])]});
            var Q2;
            Q2=makeQuery(id+"F4.imprint","IMPRINT",FACE,{"disambiguationData":[TD([[makeQuery(id+"F4.imprint","IMPRINT",EDGE,{"derivedFrom":sQuery(id+"F4.wireOp",EDGE,"E178")}),-1.0]])]});
            var Q3;
            Q3=makeQuery(id+"F5.imprint","IMPRINT",FACE,{"disambiguationData":[TD([[makeQuery(id+"F5.imprint","IMPRINT",EDGE,{"derivedFrom":sQuery(id+"F5.wireOp",EDGE,"E209")}),-1.0]])]});
            var Q4;
            Q4=makeQuery(id+"F5.imprint","IMPRINT",FACE,{"disambiguationData":[TD([[makeQuery(id+"F5.imprint","IMPRINT",EDGE,{"derivedFrom":sQuery(id+"F5.wireOp",EDGE,"E202")}),-1.0]])]});
            var Q5;
            Q5=makeQuery(id+"F5.imprint","IMPRINT",FACE,{"disambiguationData":[TD([[makeQuery(id+"F5.imprint","IMPRINT",EDGE,{"derivedFrom":sQuery(id+"F5.wireOp",EDGE,"E207")}),-1.0]])]});
            var Q6;
            Q6=makeQuery(id+"F3.imprint","IMPRINT",FACE,{"disambiguationData":[TD([[makeQuery(id+"F3.imprint","IMPRINT",EDGE,{"derivedFrom":sQuery(id+"F3.wireOp",EDGE,"E155.top")}),-1.0]])]});
            var Q7;
            Q7=makeQuery(id+"F2.imprint","IMPRINT",FACE,{"disambiguationData":[TD([[makeQuery(id+"F2.imprint","IMPRINT",EDGE,{"derivedFrom":sQuery(id+"F2.wireOp",EDGE,"E110.top")}),-1.0]])]});
            extrude(context, id + "F6", {"entities" : qUnion([Q0, Q1, Q2, Q3, Q4, Q5, Q6, Q7]), "depth" : 3.17 * mm, "offsetDistance" : 25 * mm});
        }
        {
            var Q0;
            Q0=qCreatedBy(makeId("Top.planeOp"),FACE);
            var sketch = newSketch(context, id + "F7", { "sketchPlane" : qUnion([Q0])});
            skCircle(sketch, "E232", {"center": v(915.07, 433.84) * mm, "radius": 11 * mm});
            skCircle(sketch, "E233", {"center": v(895.37, 451.72) * mm, "radius": 2.6 * mm});
            skCircle(sketch, "E234", {"center": v(915.37, 451.72) * mm, "radius": 2.6 * mm});
            skCircle(sketch, "E235", {"center": v(935.37, 451.72) * mm, "radius": 2.6 * mm});
            skLineSegment(sketch, "E236.bottom", {"start": v(895.37, 417.07) * mm, "end": v(935.37, 417.07) * mm});
            skLineSegment(sketch, "E236.top", {"start": v(895.37, 461.72) * mm, "end": v(935.37, 461.72) * mm});
            skLineSegment(sketch, "E236.left", {"start": v(890.37, 422.07) * mm, "end": v(890.37, 456.72) * mm});
            skLineSegment(sketch, "E236.right", {"start": v(940.37, 422.07) * mm, "end": v(940.37, 456.72) * mm});
            skLineSegment(sketch, "E237.bottom", {"start": v(895.17, 375.83) * mm, "end": v(935.17, 375.83) * mm});
            skLineSegment(sketch, "E237.left", {"start": v(890.17, 380.83) * mm, "end": v(890.17, 408.57) * mm});
            skLineSegment(sketch, "E237.right", {"start": v(940.17, 380.83) * mm, "end": v(940.17, 408.57) * mm});
            skCircle(sketch, "E238", {"center": v(909.2, 409.35) * mm, "radius": 1.65 * mm});
            skCircle(sketch, "E239", {"center": v(920.53, 409.35) * mm, "radius": 1.65 * mm});
            skCircle(sketch, "E240", {"center": v(920.53, 398.04) * mm, "radius": 1.65 * mm});
            skCircle(sketch, "E241", {"center": v(909.2, 398.04) * mm, "radius": 1.65 * mm});
            skCircle(sketch, "E242", {"center": v(914.87, 403.7) * mm, "radius": 5.2 * mm});
            skLineSegment(sketch, "E243.top", {"start": v(895.17, 413.57) * mm, "end": v(935.17, 413.57) * mm});
            skLineSegment(sketch, "E243.left", {"start": v(890.17, 411.26) * mm, "end": v(890.17, 413.57) * mm});
            skLineSegment(sketch, "E243.right", {"start": v(940.17, 411.26) * mm, "end": v(940.17, 413.57) * mm});
            skCircle(sketch, "E244", {"center": v(898.17, 385.54) * mm, "radius": 2.65 * mm});
            skCircle(sketch, "E245", {"center": v(932.17, 385.54) * mm, "radius": 2.65 * mm});
            skPoint(sketch, "E246.visualSharp", {"position": v(940.37, 461.72) * mm});
            skArc(sketch, "E246.filletArc", {"start": v(940.37, 456.72) * mm, "mid": v(938.9, 460.25) * mm, "end": v(935.37, 461.72) * mm});
            skPoint(sketch, "E247.visualSharp", {"position": v(890.37, 461.72) * mm});
            skArc(sketch, "E247.filletArc", {"start": v(895.37, 461.72) * mm, "mid": v(891.83, 460.25) * mm, "end": v(890.37, 456.72) * mm});
            skPoint(sketch, "E248.visualSharp", {"position": v(890.37, 417.07) * mm});
            skArc(sketch, "E248.filletArc", {"start": v(890.37, 422.07) * mm, "mid": v(891.83, 418.54) * mm, "end": v(895.37, 417.07) * mm});
            skPoint(sketch, "E249.visualSharp", {"position": v(940.37, 417.07) * mm});
            skArc(sketch, "E249.filletArc", {"start": v(935.37, 417.07) * mm, "mid": v(938.9, 418.54) * mm, "end": v(940.37, 422.07) * mm});
            skPoint(sketch, "E250.newPointA", {"position": v(940.17, 413.57) * mm});
            skPoint(sketch, "E250.newPointB", {"position": v(940.17, 411.26) * mm});
            skArc(sketch, "E250.filletArc", {"start": v(940.17, 408.57) * mm, "mid": v(938.7, 412.1) * mm, "end": v(935.17, 413.57) * mm});
            skArc(sketch, "E251.filletArc", {"start": v(895.17, 413.57) * mm, "mid": v(891.63, 412.1) * mm, "end": v(890.17, 408.57) * mm});
            skPoint(sketch, "E252.visualSharp", {"position": v(890.17, 375.83) * mm});
            skArc(sketch, "E252.filletArc", {"start": v(890.17, 380.83) * mm, "mid": v(891.63, 377.3) * mm, "end": v(895.17, 375.83) * mm});
            skPoint(sketch, "E253.visualSharp", {"position": v(940.17, 375.83) * mm});
            skArc(sketch, "E253.filletArc", {"start": v(935.17, 375.83) * mm, "mid": v(938.7, 377.3) * mm, "end": v(940.17, 380.83) * mm});
            skCircle(sketch, "E254", {"center": v(862.09, 435.79) * mm, "radius": 1.85 * mm});
            skCircle(sketch, "E255", {"center": v(862.09, 404.79) * mm, "radius": 1.85 * mm});
            skCircle(sketch, "E256", {"center": v(831.09, 404.79) * mm, "radius": 1.85 * mm});
            skCircle(sketch, "E257", {"center": v(831.09, 435.79) * mm, "radius": 1.85 * mm});
            skCircle(sketch, "E258", {"center": v(846.59, 420.29) * mm, "radius": 12.5 * mm});
            skLineSegment(sketch, "E259", {"start": v(831.09, 404.79) * mm, "end": v(862.09, 435.79) * mm, "construction": true});
            skLineSegment(sketch, "E260", {"start": v(862.09, 404.79) * mm, "end": v(831.09, 435.79) * mm, "construction": true});
            skLineSegment(sketch, "E261.bottom", {"start": v(821.59, 377.29) * mm, "end": v(871.59, 377.29) * mm});
            skCircle(sketch, "E262", {"center": v(821.59, 387.29) * mm, "radius": 2.5 * mm});
            skCircle(sketch, "E263", {"center": v(846.59, 387.29) * mm, "radius": 2.5 * mm});
            skCircle(sketch, "E264", {"center": v(871.59, 387.29) * mm, "radius": 2.5 * mm});
            skCircle(sketch, "E265", {"center": v(846.59, 420.29) * mm, "radius": 5 * mm, "construction": true});
            skLineSegment(sketch, "E266", {"start": v(841.6, 420.07) * mm, "end": v(841.6, 452.29) * mm, "construction": true});
            skLineSegment(sketch, "E267", {"start": v(851.58, 420.11) * mm, "end": v(851.58, 452.29) * mm, "construction": true});
            skLineSegment(sketch, "E268", {"start": v(821.59, 377.29) * mm, "end": v(812.68, 377.29) * mm});
            skLineSegment(sketch, "E269", {"start": v(871.59, 377.29) * mm, "end": v(880.49, 377.29) * mm});
            skLineSegment(sketch, "E270", {"start": v(885.39, 383.27) * mm, "end": v(872.39, 448.27) * mm});
            skLineSegment(sketch, "E271", {"start": v(807.78, 383.27) * mm, "end": v(820.78, 448.27) * mm});
            skArc(sketch, "E272.filletArc", {"start": v(880.49, 377.29) * mm, "mid": v(884.35, 379.12) * mm, "end": v(885.39, 383.27) * mm});
            skArc(sketch, "E273.filletArc", {"start": v(807.78, 383.27) * mm, "mid": v(808.82, 379.12) * mm, "end": v(812.68, 377.29) * mm});
            skLineSegment(sketch, "E274.top", {"start": v(825.78, 459.45) * mm, "end": v(867.39, 459.45) * mm});
            skLineSegment(sketch, "E274.left", {"start": v(820.78, 448.27) * mm, "end": v(820.78, 454.45) * mm});
            skLineSegment(sketch, "E274.right", {"start": v(872.39, 448.27) * mm, "end": v(872.39, 454.45) * mm});
            skLineSegment(sketch, "E275", {"start": v(851.58, 452.29) * mm, "end": v(851.58, 468.53) * mm, "construction": true});
            skLineSegment(sketch, "E276", {"start": v(841.6, 452.29) * mm, "end": v(841.6, 468) * mm, "construction": true});
            skCircle(sketch, "E277", {"center": v(836.44, 452.29) * mm, "radius": 2.5 * mm});
            skCircle(sketch, "E278", {"center": v(856.72, 452.29) * mm, "radius": 2.5 * mm});
            skCircle(sketch, "E279", {"center": v(836.44, 452.29) * mm, "radius": 5 * mm, "construction": true});
            skCircle(sketch, "E280", {"center": v(856.72, 452.29) * mm, "radius": 5 * mm, "construction": true});
            skArc(sketch, "E281.filletArc", {"start": v(872.39, 454.45) * mm, "mid": v(870.93, 457.99) * mm, "end": v(867.39, 459.45) * mm});
            skArc(sketch, "E282.filletArc", {"start": v(825.78, 459.45) * mm, "mid": v(822.25, 457.99) * mm, "end": v(820.78, 454.45) * mm});
            skSolve(sketch);
        }
        {
            var Q0;
            Q0=qCreatedBy(makeId("Top.planeOp"),FACE);
            var sketch = newSketch(context, id + "F8", { "sketchPlane" : qUnion([Q0])});
            skCircle(sketch, "E283", {"center": v(-345.66, 7.15) * mm, "radius": 1.59 * mm});
            skCircle(sketch, "E284", {"center": v(-325.66, 7.15) * mm, "radius": 1.59 * mm});
            skCircle(sketch, "E285", {"center": v(-345.66, -12.85) * mm, "radius": 1.59 * mm});
            skCircle(sketch, "E286", {"center": v(-325.66, -12.85) * mm, "radius": 1.59 * mm});
            skLineSegment(sketch, "E287", {"start": v(-361.18, -17.55) * mm, "end": v(-361.18, -17.6) * mm});
            skCircle(sketch, "E288", {"center": v(-303.16, 11.15) * mm, "radius": 2.05 * mm});
            skCircle(sketch, "E289", {"center": v(-303.16, -16.85) * mm, "radius": 2.05 * mm});
            skCircle(sketch, "E290", {"center": v(-368.16, -16.85) * mm, "radius": 2.05 * mm});
            skCircle(sketch, "E291", {"center": v(-368.16, 11.15) * mm, "radius": 2.05 * mm});
            skLineSegment(sketch, "E292.right", {"start": v(-363.11, 13.2) * mm, "end": v(-363.11, -18.9) * mm});
            skLineSegment(sketch, "E293.left", {"start": v(-308.21, 13.2) * mm, "end": v(-308.21, -18.9) * mm});
            skLineSegment(sketch, "E294.bottom", {"start": v(-350.25, 11.74) * mm, "end": v(-321.07, 11.74) * mm});
            skLineSegment(sketch, "E294.top", {"start": v(-350.25, -17.44) * mm, "end": v(-321.07, -17.44) * mm});
            skPoint(sketch, "E295.visualSharp", {"position": v(-308.21, 16.2) * mm});
            skPoint(sketch, "E296.visualSharp", {"position": v(-298.11, 16.2) * mm});
            skPoint(sketch, "E297.visualSharp", {"position": v(-298.11, -21.9) * mm});
            skPoint(sketch, "E298.visualSharp", {"position": v(-308.21, -21.9) * mm});
            skLineSegment(sketch, "E299", {"start": v(-350.25, -17.44) * mm, "end": v(-363.5, -17.44) * mm});
            skLineSegment(sketch, "E300", {"start": v(-350.25, 11.74) * mm, "end": v(-363.11, 11.74) * mm});
            skLineSegment(sketch, "E301", {"start": v(-321.07, 11.74) * mm, "end": v(-307.83, 11.74) * mm});
            skLineSegment(sketch, "E302", {"start": v(-321.07, -17.44) * mm, "end": v(-308.21, -17.44) * mm});
            skLineSegment(sketch, "E303.bottom", {"start": v(-368.11, 18.2) * mm, "end": v(-369.21, 18.2) * mm});
            skLineSegment(sketch, "E303.top", {"start": v(-368.11, -23.9) * mm, "end": v(-369.21, -23.9) * mm});
            skLineSegment(sketch, "E303.right", {"start": v(-374.21, 13.2) * mm, "end": v(-374.21, -18.9) * mm});
            skLineSegment(sketch, "E304.bottom", {"start": v(-303.21, -23.9) * mm, "end": v(-302.11, -23.9) * mm});
            skLineSegment(sketch, "E304.top", {"start": v(-303.21, 18.2) * mm, "end": v(-302.11, 18.2) * mm});
            skLineSegment(sketch, "E304.left", {"start": v(-308.21, -18.9) * mm, "end": v(-308.21, 13.2) * mm});
            skLineSegment(sketch, "E304.right", {"start": v(-297.11, -18.9) * mm, "end": v(-297.11, 13.2) * mm});
            skPoint(sketch, "E305.visualSharp", {"position": v(-374.21, 18.2) * mm});
            skArc(sketch, "E305.filletArc", {"start": v(-369.21, 18.2) * mm, "mid": v(-372.75, 16.74) * mm, "end": v(-374.21, 13.2) * mm});
            skPoint(sketch, "E306.visualSharp", {"position": v(-363.11, 18.2) * mm});
            skArc(sketch, "E306.filletArc", {"start": v(-363.11, 13.2) * mm, "mid": v(-364.58, 16.74) * mm, "end": v(-368.11, 18.2) * mm});
            skPoint(sketch, "E307.visualSharp", {"position": v(-374.21, -23.9) * mm});
            skArc(sketch, "E307.filletArc", {"start": v(-374.21, -18.9) * mm, "mid": v(-372.75, -22.43) * mm, "end": v(-369.21, -23.9) * mm});
            skPoint(sketch, "E308.visualSharp", {"position": v(-363.11, -23.9) * mm});
            skArc(sketch, "E308.filletArc", {"start": v(-368.11, -23.9) * mm, "mid": v(-364.58, -22.43) * mm, "end": v(-363.11, -18.9) * mm});
            skPoint(sketch, "E309.visualSharp", {"position": v(-308.21, 18.2) * mm});
            skArc(sketch, "E309.filletArc", {"start": v(-303.21, 18.2) * mm, "mid": v(-306.75, 16.74) * mm, "end": v(-308.21, 13.2) * mm});
            skPoint(sketch, "E310.visualSharp", {"position": v(-297.11, 18.2) * mm});
            skArc(sketch, "E310.filletArc", {"start": v(-297.11, 13.2) * mm, "mid": v(-298.58, 16.74) * mm, "end": v(-302.11, 18.2) * mm});
            skPoint(sketch, "E311.visualSharp", {"position": v(-297.11, -23.9) * mm});
            skArc(sketch, "E311.filletArc", {"start": v(-302.11, -23.9) * mm, "mid": v(-298.58, -22.43) * mm, "end": v(-297.11, -18.9) * mm});
            skPoint(sketch, "E312.visualSharp", {"position": v(-308.21, -23.9) * mm});
            skArc(sketch, "E312.filletArc", {"start": v(-308.21, -18.9) * mm, "mid": v(-306.75, -22.43) * mm, "end": v(-303.21, -23.9) * mm});
            skSolve(sketch);
        }
        {
            var Q0;
            Q0 = qSketchRegion(id + "F8", true);
            extrude(context, id + "F9", {"entities" : qUnion([Q0]), "depth" : 3.17 * mm, "offsetDistance" : 25 * mm});
        }
        {
            var Q0;
            Q0=makeQuery(id+"F9.opExtrude","CAP_FACE",FACE,{"disambiguationData":[OSD([sQuery(id+"F8.wireOp",EDGE,"E283"),sQuery(id+"F8.wireOp",EDGE,"E284"),sQuery(id+"F8.wireOp",EDGE,"E285"),sQuery(id+"F8.wireOp",EDGE,"E286"),sQuery(id+"F8.wireOp",EDGE,"E288"),sQuery(id+"F8.wireOp",EDGE,"E289"),sQuery(id+"F8.wireOp",EDGE,"E290"),sQuery(id+"F8.wireOp",EDGE,"E291"),sQuery(id+"F8.wireOp",EDGE,"E292.right"),sQuery(id+"F8.wireOp",EDGE,"E293.left"),sQuery(id+"F8.wireOp",EDGE,"E294.bottom"),sQuery(id+"F8.wireOp",EDGE,"E294.top"),sQuery(id+"F8.wireOp",EDGE,"E299"),sQuery(id+"F8.wireOp",EDGE,"E300"),sQuery(id+"F8.wireOp",EDGE,"E301"),sQuery(id+"F8.wireOp",EDGE,"E302"),sQuery(id+"F8.wireOp",EDGE,"E303.bottom"),sQuery(id+"F8.wireOp",EDGE,"E303.top"),sQuery(id+"F8.wireOp",EDGE,"E303.right"),sQuery(id+"F8.wireOp",EDGE,"E304.bottom"),sQuery(id+"F8.wireOp",EDGE,"E304.top"),sQuery(id+"F8.wireOp",EDGE,"E304.right"),sQuery(id+"F8.wireOp",EDGE,"E305.filletArc"),sQuery(id+"F8.wireOp",EDGE,"E306.filletArc"),sQuery(id+"F8.wireOp",EDGE,"E307.filletArc"),sQuery(id+"F8.wireOp",EDGE,"E308.filletArc"),sQuery(id+"F8.wireOp",EDGE,"E309.filletArc"),sQuery(id+"F8.wireOp",EDGE,"E310.filletArc"),sQuery(id+"F8.wireOp",EDGE,"E311.filletArc"),sQuery(id+"F8.wireOp",EDGE,"E312.filletArc")])],"isStart":false});
            var sketch = newSketch(context, id + "F10", { "sketchPlane" : qUnion([Q0])});
            skCircle(sketch, "E313", {"center": v(-345.66, 7.15) * mm, "radius": 1.59 * mm});
            skCircle(sketch, "E314", {"center": v(-325.66, 7.15) * mm, "radius": 1.59 * mm});
            skCircle(sketch, "E315", {"center": v(-345.66, -12.85) * mm, "radius": 1.59 * mm});
            skCircle(sketch, "E316", {"center": v(-325.66, -12.85) * mm, "radius": 1.59 * mm});
            skLineSegment(sketch, "E317.bottom", {"start": v(-352.66, 11.74) * mm, "end": v(-318.66, 11.74) * mm});
            skLineSegment(sketch, "E317.top", {"start": v(-352.66, -17.44) * mm, "end": v(-318.66, -17.44) * mm});
            skLineSegment(sketch, "E317.left", {"start": v(-352.66, 11.74) * mm, "end": v(-352.66, -17.44) * mm});
            skLineSegment(sketch, "E317.right", {"start": v(-318.66, 11.74) * mm, "end": v(-318.66, -17.44) * mm});
            skLineSegment(sketch, "E318.bottom", {"start": v(-352.66, -9.44) * mm, "end": v(-374.21, -9.44) * mm});
            skLineSegment(sketch, "E318.top", {"start": v(-352.66, 3.74) * mm, "end": v(-374.21, 3.74) * mm});
            skLineSegment(sketch, "E318.left", {"start": v(-352.66, -9.44) * mm, "end": v(-352.66, 3.74) * mm});
            skLineSegment(sketch, "E318.right", {"start": v(-374.21, -9.44) * mm, "end": v(-374.21, 3.74) * mm});
            skLineSegment(sketch, "E319.bottom", {"start": v(-352.66, -17.44) * mm, "end": v(-360.66, -17.44) * mm});
            skLineSegment(sketch, "E319.top", {"start": v(-352.66, -9.44) * mm, "end": v(-360.66, -9.44) * mm});
            skLineSegment(sketch, "E319.left", {"start": v(-352.66, -17.44) * mm, "end": v(-352.66, -9.44) * mm});
            skLineSegment(sketch, "E319.right", {"start": v(-360.66, -17.44) * mm, "end": v(-360.66, -9.44) * mm});
            skLineSegment(sketch, "E320.bottom", {"start": v(-318.66, -9.6) * mm, "end": v(-310.66, -9.6) * mm});
            skLineSegment(sketch, "E320.top", {"start": v(-318.66, -17.44) * mm, "end": v(-310.66, -17.44) * mm});
            skLineSegment(sketch, "E320.left", {"start": v(-318.66, -9.6) * mm, "end": v(-318.66, -17.44) * mm});
            skLineSegment(sketch, "E320.right", {"start": v(-310.66, -9.6) * mm, "end": v(-310.66, -17.44) * mm});
            skSolve(sketch);
        }
        {
            var Q0;
            {var subQ2=sQuery(id+"F10.wireOp",EDGE,"E320.bottom");Q0=makeQuery(id+"F10.imprint","IMPRINT",FACE,{"disambiguationData":[TD([[makeQuery(id+"F10.imprint","IMPRINT",EDGE,{"derivedFrom":subQ2}),-1.0]])]});}
            var Q1;
            {var subQ0=sQuery(id+"F10.wireOp",EDGE,"E319.bottom");Q1=makeQuery(id+"F10.imprint","IMPRINT",FACE,{"disambiguationData":[TD([[makeQuery(id+"F10.imprint","IMPRINT",EDGE,{"derivedFrom":subQ0}),-1.0]])]});}
            var Q2;
            Q2=makeQuery(id+"F10.imprint","IMPRINT",FACE,{"disambiguationData":[TD([[makeQuery(id+"F10.imprint","IMPRINT",EDGE,{"derivedFrom":sQuery(id+"F10.wireOp",EDGE,"E313")}),-1.0]])]});
            extrude(context, id + "F11", {"entities" : qUnion([Q0, Q1, Q2]), "depth" : 5 * mm, "offsetDistance" : 25 * mm});
        }
        {
            var Q0;
            Q0=makeQuery(id+"F11.opExtrude","CAP_FACE",FACE,{"disambiguationData":[OSD([sQuery(id+"F10.wireOp",EDGE,"E313"),sQuery(id+"F10.wireOp",EDGE,"E314"),sQuery(id+"F10.wireOp",EDGE,"E315"),sQuery(id+"F10.wireOp",EDGE,"E316"),sQuery(id+"F10.wireOp",EDGE,"E317.bottom"),sQuery(id+"F10.wireOp",EDGE,"E317.top"),sQuery(id+"F10.wireOp",EDGE,"E317.left"),sQuery(id+"F10.wireOp",EDGE,"E317.right")])],"isStart":false});
            var sketch = newSketch(context, id + "F12", { "sketchPlane" : qUnion([Q0])});
            skLineSegment(sketch, "E321.bottom", {"start": v(-352.66, 10.56) * mm, "end": v(-318.66, 10.56) * mm});
            skLineSegment(sketch, "E321.top", {"start": v(-352.66, 13.73) * mm, "end": v(-318.66, 13.73) * mm});
            skLineSegment(sketch, "E321.left", {"start": v(-352.66, 10.56) * mm, "end": v(-352.66, 13.73) * mm});
            skLineSegment(sketch, "E321.right", {"start": v(-318.66, 10.56) * mm, "end": v(-318.66, 13.73) * mm});
            skSolve(sketch);
        }
        {
            var Q0;
            Q0 = qSketchRegion(id + "F12", true);
            extrude(context, id + "F13", {"entities" : qUnion([Q0]), "operationType" : NewBodyOperationType.ADD, "depth" : 45 * mm, "offsetDistance" : 25 * mm});
        }
        {
            var Q0;
            Q0=makeQuery(id+"F13.opExtrude","CAP_FACE",FACE,{"disambiguationData":[OSD([sQuery(id+"F12.wireOp",EDGE,"E321.bottom"),sQuery(id+"F12.wireOp",EDGE,"E321.top"),sQuery(id+"F12.wireOp",EDGE,"E321.left"),sQuery(id+"F12.wireOp",EDGE,"E321.right")])],"isStart":true});
            extrude(context, id + "F14", {"entities" : qUnion([Q0]), "operationType" : NewBodyOperationType.ADD, "depth" : 5 * mm, "offsetDistance" : 25 * mm});
        }
        {
            var Q0;
            {var subQ0=sQuery(id+"F12.wireOp",EDGE,"E321.top");Q0=makeQuery(id+"F14.boolean.opBoolean","MERGE",FACE,{"derivedFrom":[makeQuery(id+"F13.opExtrude","SWEPT_FACE",FACE,{"disambiguationData":[OSD([subQ0])]}),makeQuery(id+"F14.opExtrude","SWEPT_FACE",FACE,{"disambiguationData":[OSD([subQ0])]})]});}
            var sketch = newSketch(context, id + "F15", { "sketchPlane" : qUnion([Q0])});
            skCircle(sketch, "E322", {"center": v(351.21, 48.72) * mm, "radius": 1.85 * mm});
            skCircle(sketch, "E323", {"center": v(351.21, 17.63) * mm, "radius": 1.85 * mm});
            skCircle(sketch, "E324", {"center": v(320.21, 17.72) * mm, "radius": 1.85 * mm});
            skCircle(sketch, "E325", {"center": v(320.21, 48.63) * mm, "radius": 1.85 * mm});
            skCircle(sketch, "E326", {"center": v(335.66, 33.17) * mm, "radius": 11.75 * mm});
            skLineSegment(sketch, "E327", {"start": v(335.66, 3.18) * mm, "end": v(335.66, 53.17) * mm});
            skLineSegment(sketch, "E328", {"start": v(320.21, 17.72) * mm, "end": v(351.21, 48.72) * mm, "construction": true});
            skLineSegment(sketch, "E329", {"start": v(351.21, 17.63) * mm, "end": v(320.21, 48.63) * mm, "construction": true});
            skSolve(sketch);
        }
        {
            var Q0;
            {var subQ0=sQuery(id+"F12.wireOp",EDGE,"E321.left");Q0=makeQuery(id+"F14.boolean.opBoolean","MERGE",FACE,{"derivedFrom":[makeQuery(id+"F13.boolean.opBoolean","MERGE",FACE,{"derivedFrom":[makeQuery(id+"F11.opExtrude","SWEPT_FACE",FACE,{"disambiguationData":[OSD([sQuery(id+"F10.wireOp",EDGE,"E317.left")])]}),makeQuery(id+"F13.opExtrude","SWEPT_FACE",FACE,{"disambiguationData":[OSD([subQ0])]})]}),makeQuery(id+"F14.opExtrude","SWEPT_FACE",FACE,{"disambiguationData":[OSD([subQ0])]})]});}
            extrude(context, id + "F16", {"entities" : qUnion([Q0]), "operationType" : NewBodyOperationType.ADD, "depth" : 5 * mm, "offsetDistance" : 25 * mm});
        }
        {
            var Q0;
            {var subQ0=sQuery(id+"F12.wireOp",EDGE,"E321.right");Q0=makeQuery(id+"F14.boolean.opBoolean","MERGE",FACE,{"derivedFrom":[makeQuery(id+"F13.boolean.opBoolean","MERGE",FACE,{"derivedFrom":[makeQuery(id+"F11.opExtrude","SWEPT_FACE",FACE,{"disambiguationData":[OSD([sQuery(id+"F10.wireOp",EDGE,"E317.right")])]}),makeQuery(id+"F13.opExtrude","SWEPT_FACE",FACE,{"disambiguationData":[OSD([subQ0])]})]}),makeQuery(id+"F14.opExtrude","SWEPT_FACE",FACE,{"disambiguationData":[OSD([subQ0])]})]});}
            extrude(context, id + "F17", {"entities" : qUnion([Q0]), "operationType" : NewBodyOperationType.ADD, "depth" : 5 * mm, "offsetDistance" : 25 * mm});
        }
        {
            var Q0;
            {var subQ0=sQuery(id+"F15.wireOp",EDGE,"E327");var subQ1=sQuery(id+"F15.wireOp",EDGE,"E326");var subQ2=makeQuery(id+"F15.imprint","INTERSECT",VERTEX,{"disambiguationData":[OD(0.0)],"derivedFrom":[subQ1,subQ0]});Q0=makeQuery(id+"F15.imprint","IMPRINT",FACE,{"disambiguationData":[TD([[makeQuery(id+"F15.imprint","IMPRINT",EDGE,{"disambiguationData":[TD([[subQ2,-1.0]])],"derivedFrom":subQ1}),1.0]])]});}
            var Q1;
            {var subQ0=sQuery(id+"F15.wireOp",EDGE,"E327");var subQ1=sQuery(id+"F15.wireOp",EDGE,"E326");var subQ2=makeQuery(id+"F15.imprint","INTERSECT",VERTEX,{"disambiguationData":[OD(0.0)],"derivedFrom":[subQ1,subQ0]});Q1=makeQuery(id+"F15.imprint","IMPRINT",FACE,{"disambiguationData":[TD([[makeQuery(id+"F15.imprint","IMPRINT",EDGE,{"disambiguationData":[TD([[subQ2,1.0]])],"derivedFrom":subQ1}),1.0]])]});}
            var Q2;
            {var subQ0=sQuery(id+"F15.wireOp",EDGE,"E324");var subQ1=sQuery(id+"F12.wireOp",EDGE,"E321.right");var subQ2=sQuery(id+"F12.wireOp",EDGE,"E321.top");var subQ3=makeQuery(id+"F14.boolean.opBoolean","MERGE",EDGE,{"derivedFrom":[makeQuery(id+"F13.opExtrude","SWEPT_EDGE",EDGE,{"disambiguationData":[OSD([subQ2,subQ1])]}),makeQuery(id+"F14.opExtrude","SWEPT_EDGE",EDGE,{"disambiguationData":[OSD([subQ2,subQ1])]})]});var subQ4=makeQuery(id+"F15.imprint","INTERSECT",VERTEX,{"disambiguationData":[OD(0.0)],"derivedFrom":[subQ3,subQ0]});Q2=makeQuery(id+"F15.imprint","IMPRINT",FACE,{"disambiguationData":[TD([[makeQuery(id+"F15.imprint","IMPRINT",EDGE,{"disambiguationData":[TD([[subQ4,-1.0]])],"derivedFrom":subQ0}),1.0]])]});}
            var Q3;
            {var subQ0=sQuery(id+"F15.wireOp",EDGE,"E323");var subQ1=sQuery(id+"F12.wireOp",EDGE,"E321.left");var subQ2=sQuery(id+"F12.wireOp",EDGE,"E321.top");var subQ3=makeQuery(id+"F14.boolean.opBoolean","MERGE",EDGE,{"derivedFrom":[makeQuery(id+"F13.opExtrude","SWEPT_EDGE",EDGE,{"disambiguationData":[OSD([subQ2,subQ1])]}),makeQuery(id+"F14.opExtrude","SWEPT_EDGE",EDGE,{"disambiguationData":[OSD([subQ2,subQ1])]})]});var subQ4=makeQuery(id+"F15.imprint","INTERSECT",VERTEX,{"disambiguationData":[OD(0.0)],"derivedFrom":[subQ3,subQ0]});Q3=makeQuery(id+"F15.imprint","IMPRINT",FACE,{"disambiguationData":[TD([[makeQuery(id+"F15.imprint","IMPRINT",EDGE,{"disambiguationData":[TD([[subQ4,1.0]])],"derivedFrom":subQ0}),1.0]])]});}
            var Q4;
            {var subQ0=sQuery(id+"F15.wireOp",EDGE,"E325");var subQ1=sQuery(id+"F12.wireOp",EDGE,"E321.right");var subQ2=sQuery(id+"F12.wireOp",EDGE,"E321.top");var subQ3=makeQuery(id+"F14.boolean.opBoolean","MERGE",EDGE,{"derivedFrom":[makeQuery(id+"F13.opExtrude","SWEPT_EDGE",EDGE,{"disambiguationData":[OSD([subQ2,subQ1])]}),makeQuery(id+"F14.opExtrude","SWEPT_EDGE",EDGE,{"disambiguationData":[OSD([subQ2,subQ1])]})]});var subQ4=makeQuery(id+"F15.imprint","INTERSECT",VERTEX,{"disambiguationData":[OD(0.0)],"derivedFrom":[subQ3,subQ0]});Q4=makeQuery(id+"F15.imprint","IMPRINT",FACE,{"disambiguationData":[TD([[makeQuery(id+"F15.imprint","IMPRINT",EDGE,{"disambiguationData":[TD([[subQ4,1.0]])],"derivedFrom":subQ0}),1.0]])]});}
            var Q5;
            {var subQ0=sQuery(id+"F15.wireOp",EDGE,"E322");var subQ1=sQuery(id+"F12.wireOp",EDGE,"E321.left");var subQ2=sQuery(id+"F12.wireOp",EDGE,"E321.top");var subQ3=makeQuery(id+"F14.boolean.opBoolean","MERGE",EDGE,{"derivedFrom":[makeQuery(id+"F13.opExtrude","SWEPT_EDGE",EDGE,{"disambiguationData":[OSD([subQ2,subQ1])]}),makeQuery(id+"F14.opExtrude","SWEPT_EDGE",EDGE,{"disambiguationData":[OSD([subQ2,subQ1])]})]});var subQ4=makeQuery(id+"F15.imprint","INTERSECT",VERTEX,{"disambiguationData":[OD(0.0)],"derivedFrom":[subQ3,subQ0]});Q5=makeQuery(id+"F15.imprint","IMPRINT",FACE,{"disambiguationData":[TD([[makeQuery(id+"F15.imprint","IMPRINT",EDGE,{"disambiguationData":[TD([[subQ4,-1.0]])],"derivedFrom":subQ0}),1.0]])]});}
            var Q6;
            {var subQ0=sQuery(id+"F15.wireOp",EDGE,"E324");var subQ1=sQuery(id+"F12.wireOp",EDGE,"E321.right");var subQ2=sQuery(id+"F12.wireOp",EDGE,"E321.top");var subQ3=makeQuery(id+"F14.boolean.opBoolean","MERGE",EDGE,{"derivedFrom":[makeQuery(id+"F13.opExtrude","SWEPT_EDGE",EDGE,{"disambiguationData":[OSD([subQ2,subQ1])]}),makeQuery(id+"F14.opExtrude","SWEPT_EDGE",EDGE,{"disambiguationData":[OSD([subQ2,subQ1])]})]});var subQ4=makeQuery(id+"F15.imprint","INTERSECT",VERTEX,{"disambiguationData":[OD(0.0)],"derivedFrom":[subQ3,subQ0]});Q6=makeQuery(id+"F15.imprint","IMPRINT",FACE,{"disambiguationData":[TD([[makeQuery(id+"F15.imprint","IMPRINT",EDGE,{"disambiguationData":[TD([[subQ4,1.0]])],"derivedFrom":subQ0}),1.0]])]});}
            var Q7;
            {var subQ0=sQuery(id+"F15.wireOp",EDGE,"E325");var subQ1=sQuery(id+"F12.wireOp",EDGE,"E321.right");var subQ2=sQuery(id+"F12.wireOp",EDGE,"E321.top");var subQ3=makeQuery(id+"F14.boolean.opBoolean","MERGE",EDGE,{"derivedFrom":[makeQuery(id+"F13.opExtrude","SWEPT_EDGE",EDGE,{"disambiguationData":[OSD([subQ2,subQ1])]}),makeQuery(id+"F14.opExtrude","SWEPT_EDGE",EDGE,{"disambiguationData":[OSD([subQ2,subQ1])]})]});var subQ4=makeQuery(id+"F15.imprint","INTERSECT",VERTEX,{"disambiguationData":[OD(0.0)],"derivedFrom":[subQ3,subQ0]});Q7=makeQuery(id+"F15.imprint","IMPRINT",FACE,{"disambiguationData":[TD([[makeQuery(id+"F15.imprint","IMPRINT",EDGE,{"disambiguationData":[TD([[subQ4,-1.0]])],"derivedFrom":subQ0}),1.0]])]});}
            var Q8;
            {var subQ0=sQuery(id+"F15.wireOp",EDGE,"E323");var subQ1=sQuery(id+"F12.wireOp",EDGE,"E321.left");var subQ2=sQuery(id+"F12.wireOp",EDGE,"E321.top");var subQ3=makeQuery(id+"F14.boolean.opBoolean","MERGE",EDGE,{"derivedFrom":[makeQuery(id+"F13.opExtrude","SWEPT_EDGE",EDGE,{"disambiguationData":[OSD([subQ2,subQ1])]}),makeQuery(id+"F14.opExtrude","SWEPT_EDGE",EDGE,{"disambiguationData":[OSD([subQ2,subQ1])]})]});var subQ4=makeQuery(id+"F15.imprint","INTERSECT",VERTEX,{"disambiguationData":[OD(0.0)],"derivedFrom":[subQ3,subQ0]});Q8=makeQuery(id+"F15.imprint","IMPRINT",FACE,{"disambiguationData":[TD([[makeQuery(id+"F15.imprint","IMPRINT",EDGE,{"disambiguationData":[TD([[subQ4,-1.0]])],"derivedFrom":subQ0}),1.0]])]});}
            var Q9;
            {var subQ0=sQuery(id+"F15.wireOp",EDGE,"E322");var subQ1=sQuery(id+"F12.wireOp",EDGE,"E321.left");var subQ2=sQuery(id+"F12.wireOp",EDGE,"E321.top");var subQ3=makeQuery(id+"F14.boolean.opBoolean","MERGE",EDGE,{"derivedFrom":[makeQuery(id+"F13.opExtrude","SWEPT_EDGE",EDGE,{"disambiguationData":[OSD([subQ2,subQ1])]}),makeQuery(id+"F14.opExtrude","SWEPT_EDGE",EDGE,{"disambiguationData":[OSD([subQ2,subQ1])]})]});var subQ4=makeQuery(id+"F15.imprint","INTERSECT",VERTEX,{"disambiguationData":[OD(0.0)],"derivedFrom":[subQ3,subQ0]});Q9=makeQuery(id+"F15.imprint","IMPRINT",FACE,{"disambiguationData":[TD([[makeQuery(id+"F15.imprint","IMPRINT",EDGE,{"disambiguationData":[TD([[subQ4,1.0]])],"derivedFrom":subQ0}),1.0]])]});}
            extrude(context, id + "F18", {"entities" : qUnion([Q0, Q1, Q2, Q3, Q4, Q5, Q6, Q7, Q8, Q9]), "operationType" : NewBodyOperationType.REMOVE, "oppositeDirection" : true, "depth" : 25 * mm, "offsetDistance" : 25 * mm});
        }
        {
            var Q0;
            Q0=makeQuery(id+"F9.opExtrude","SWEPT_FACE",FACE,{"disambiguationData":[OSD([sQuery(id+"F8.wireOp",EDGE,"E303.right")])]});
            var sketch = newSketch(context, id + "F19", { "sketchPlane" : qUnion([Q0])});
            skLineSegment(sketch, "E330.bottom", {"start": v(8.44, -13) * mm, "end": v(-2.74, -13) * mm});
            skLineSegment(sketch, "E330.top", {"start": v(8.44, 22.35) * mm, "end": v(-2.74, 22.35) * mm});
            skLineSegment(sketch, "E330.left", {"start": v(8.44, -13) * mm, "end": v(8.44, 22.35) * mm});
            skLineSegment(sketch, "E330.right", {"start": v(-2.74, -13) * mm, "end": v(-2.74, 22.35) * mm});
            skCircle(sketch, "E331", {"center": v(2.85, -9.41) * mm, "radius": 1.59 * mm});
            skCircle(sketch, "E332", {"center": v(2.85, 18.76) * mm, "radius": 1.59 * mm});
            skLineSegment(sketch, "E333", {"start": v(2.85, 0) * mm, "end": v(2.85, 3.17) * mm});
            skPoint(sketch, "E334", {"position": v(2.85, 1.59) * mm});
            skCircle(sketch, "E335", {"center": v(5.85, 5.92) * mm, "radius": 1.59 * mm});
            skCircle(sketch, "E336", {"center": v(-0.15, 5.92) * mm, "radius": 1.59 * mm});
            skSolve(sketch);
        }
        {
            var Q0;
            {var subQ1=sQuery(id+"F19.wireOp",EDGE,"E330.bottom");Q0=makeQuery(id+"F19.imprint","IMPRINT",FACE,{"disambiguationData":[TD([[makeQuery(id+"F19.imprint","IMPRINT",EDGE,{"derivedFrom":subQ1}),-1.0]])]});}
            var Q1;
            {var subQ1=sQuery(id+"F19.wireOp",EDGE,"E330.top");Q1=makeQuery(id+"F19.imprint","IMPRINT",FACE,{"disambiguationData":[TD([[makeQuery(id+"F19.imprint","IMPRINT",EDGE,{"derivedFrom":subQ1}),1.0]])]});}
            var Q2;
            {var subQ6=sQuery(id+"F19.wireOp",EDGE,"E333");Q2=makeQuery(id+"F19.imprint","IMPRINT",FACE,{"disambiguationData":[TD([[makeQuery(id+"F19.imprint","IMPRINT",EDGE,{"derivedFrom":subQ6}),1.0]])]});}
            var Q3;
            {var subQ6=sQuery(id+"F19.wireOp",EDGE,"E333");Q3=makeQuery(id+"F19.imprint","IMPRINT",FACE,{"disambiguationData":[TD([[makeQuery(id+"F19.imprint","IMPRINT",EDGE,{"derivedFrom":subQ6}),-1.0]])]});}
            extrude(context, id + "F20", {"entities" : qUnion([Q0, Q1, Q2, Q3]), "depth" : 3 * mm, "offsetDistance" : 25 * mm});
        }
        {
            var Q0;
            Q0=makeQuery(id+"F20.opExtrude","CAP_FACE",FACE,{"disambiguationData":[OSD([sQuery(id+"F19.wireOp",EDGE,"E330.bottom"),sQuery(id+"F19.wireOp",EDGE,"E330.top"),sQuery(id+"F19.wireOp",EDGE,"E330.left"),sQuery(id+"F19.wireOp",EDGE,"E330.right"),sQuery(id+"F19.wireOp",EDGE,"E331"),sQuery(id+"F19.wireOp",EDGE,"E332")])],"isStart":false});
            var sketch = newSketch(context, id + "F21", { "sketchPlane" : qUnion([Q0])});
            skCircle(sketch, "E337", {"center": v(2.85, -9.41) * mm, "radius": 1.59 * mm});
            skCircle(sketch, "E338", {"center": v(2.85, 18.76) * mm, "radius": 1.59 * mm});
            skCircle(sketch, "E339", {"center": v(2.85, 18.76) * mm, "radius": 2.5 * mm});
            skCircle(sketch, "E340", {"center": v(2.85, -9.41) * mm, "radius": 2.5 * mm});
            skSolve(sketch);
        }
        {
            var Q0;
            Q0=makeQuery(id+"F21.imprint","IMPRINT",FACE,{"disambiguationData":[TD([[makeQuery(id+"F21.imprint","IMPRINT",EDGE,{"derivedFrom":sQuery(id+"F21.wireOp",EDGE,"E338")}),-1.0]])]});
            var Q1;
            Q1=makeQuery(id+"F21.imprint","IMPRINT",FACE,{"disambiguationData":[TD([[makeQuery(id+"F21.imprint","IMPRINT",EDGE,{"derivedFrom":sQuery(id+"F21.wireOp",EDGE,"E337")}),-1.0]])]});
            extrude(context, id + "F22", {"entities" : qUnion([Q0, Q1]), "operationType" : NewBodyOperationType.ADD, "depth" : 4.5 * mm, "offsetDistance" : 25 * mm});
        }
        {
            var Q0;
            Q0=makeQuery(id+"F16.opExtrude","CAP_FACE",FACE,{"disambiguationData":[OSD([sQuery(id+"F10.wireOp",EDGE,"E317.left"),sQuery(id+"F12.wireOp",EDGE,"E321.left")])],"isStart":false});
            var sketch = newSketch(context, id + "F23", { "sketchPlane" : qUnion([Q0])});
            skSolve(sketch);
        }
        {
            var Q0;
            Q0=makeQuery(id+"F20.opExtrude","CAP_FACE",FACE,{"disambiguationData":[OSD([sQuery(id+"F19.wireOp",EDGE,"E330.bottom"),sQuery(id+"F19.wireOp",EDGE,"E330.top"),sQuery(id+"F19.wireOp",EDGE,"E330.left"),sQuery(id+"F19.wireOp",EDGE,"E330.right"),sQuery(id+"F19.wireOp",EDGE,"E331"),sQuery(id+"F19.wireOp",EDGE,"E332"),sQuery(id+"F19.wireOp",EDGE,"E335"),sQuery(id+"F19.wireOp",EDGE,"E336")])],"isStart":false});
            var sketch = newSketch(context, id + "F24", { "sketchPlane" : qUnion([Q0])});
            skCircle(sketch, "E341", {"center": v(-0.15, 5.92) * mm, "radius": 1.4 * mm});
            skCircle(sketch, "E342", {"center": v(5.85, 5.92) * mm, "radius": 1.4 * mm});
            skSolve(sketch);
        }
        {
            var Q0;
            Q0=makeQuery(id+"F24.imprint","IMPRINT",FACE,{"disambiguationData":[TD([[makeQuery(id+"F24.imprint","IMPRINT",EDGE,{"derivedFrom":sQuery(id+"F24.wireOp",EDGE,"E341")}),1.0]])]});
            var Q1;
            Q1=makeQuery(id+"F24.imprint","IMPRINT",FACE,{"disambiguationData":[TD([[makeQuery(id+"F24.imprint","IMPRINT",EDGE,{"derivedFrom":sQuery(id+"F24.wireOp",EDGE,"E342")}),1.0]])]});
            extrude(context, id + "F25", {"entities" : qUnion([Q0, Q1]), "operationType" : NewBodyOperationType.REMOVE, "oppositeDirection" : true, "depth" : 8 * mm, "offsetDistance" : 25 * mm});
        }
        {
            var Q0;
            Q0=makeQuery(id+"F7.imprint","IMPRINT",FACE,{"disambiguationData":[TD([[makeQuery(id+"F7.imprint","IMPRINT",EDGE,{"derivedFrom":sQuery(id+"F7.wireOp",EDGE,"E232")}),-1.0]])]});
            var Q1;
            Q1=makeQuery(id+"F7.imprint","IMPRINT",FACE,{"disambiguationData":[TD([[makeQuery(id+"F7.imprint","IMPRINT",EDGE,{"derivedFrom":sQuery(id+"F7.wireOp",EDGE,"E237.bottom")}),1.0]])]});
            extrude(context, id + "F26", {"entities" : qUnion([Q0, Q1]), "depth" : 3.17 * mm, "offsetDistance" : 25 * mm});
        }
        {
            var Q0;
            Q0=qCreatedBy(makeId("Top.planeOp"),FACE);
            var sketch = newSketch(context, id + "F27", { "sketchPlane" : qUnion([Q0])});
            skCircle(sketch, "E343", {"center": v(-382.42, -230.32) * mm, "radius": 1.85 * mm});
            skCircle(sketch, "E344", {"center": v(-382.42, -261.32) * mm, "radius": 1.85 * mm});
            skCircle(sketch, "E345", {"center": v(-413.42, -261.32) * mm, "radius": 1.85 * mm});
            skCircle(sketch, "E346", {"center": v(-413.42, -230.32) * mm, "radius": 1.85 * mm});
            skCircle(sketch, "E347", {"center": v(-397.92, -245.82) * mm, "radius": 12.5 * mm});
            skLineSegment(sketch, "E348", {"start": v(-413.42, -261.32) * mm, "end": v(-382.42, -230.32) * mm, "construction": true});
            skLineSegment(sketch, "E349", {"start": v(-382.42, -261.32) * mm, "end": v(-413.42, -230.32) * mm, "construction": true});
            skLineSegment(sketch, "E350.bottom", {"start": v(-422.92, -288.82) * mm, "end": v(-372.92, -288.82) * mm});
            skLineSegment(sketch, "E350.top", {"start": v(-418.82, -213.82) * mm, "end": v(-377.02, -213.82) * mm});
            skLineSegment(sketch, "E350.left", {"start": v(-422.92, -288.82) * mm, "end": v(-422.92, -213.82) * mm});
            skLineSegment(sketch, "E350.right", {"start": v(-372.92, -288.82) * mm, "end": v(-372.92, -213.82) * mm});
            skCircle(sketch, "E351", {"center": v(-422.92, -278.82) * mm, "radius": 2.5 * mm});
            skCircle(sketch, "E352", {"center": v(-397.92, -278.82) * mm, "radius": 2.5 * mm});
            skCircle(sketch, "E353", {"center": v(-372.92, -278.82) * mm, "radius": 2.5 * mm});
            skLineSegment(sketch, "E354", {"start": v(-422.92, -270.15) * mm, "end": v(-372.92, -270.15) * mm, "construction": true});
            skLineSegment(sketch, "E355", {"start": v(-422.92, -223.82) * mm, "end": v(-372.92, -223.82) * mm, "construction": true});
            skCircle(sketch, "E356", {"center": v(-397.92, -245.82) * mm, "radius": 5 * mm, "construction": true});
            skLineSegment(sketch, "E357", {"start": v(-402.92, -246.04) * mm, "end": v(-402.92, -213.82) * mm, "construction": true});
            skLineSegment(sketch, "E358", {"start": v(-392.93, -246) * mm, "end": v(-392.93, -213.82) * mm, "construction": true});
            skLineSegment(sketch, "E359", {"start": v(-422.92, -288.82) * mm, "end": v(-431.82, -288.82) * mm});
            skLineSegment(sketch, "E360", {"start": v(-372.92, -288.82) * mm, "end": v(-364.02, -288.82) * mm});
            skLineSegment(sketch, "E361", {"start": v(-359.12, -282.84) * mm, "end": v(-372.12, -217.84) * mm});
            skLineSegment(sketch, "E362", {"start": v(-436.73, -282.84) * mm, "end": v(-423.73, -217.84) * mm});
            skPoint(sketch, "E363.visualSharp", {"position": v(-422.92, -213.82) * mm});
            skArc(sketch, "E363.filletArc", {"start": v(-418.82, -213.82) * mm, "mid": v(-422, -214.95) * mm, "end": v(-423.73, -217.84) * mm});
            skPoint(sketch, "E364.visualSharp", {"position": v(-372.92, -213.82) * mm});
            skArc(sketch, "E364.filletArc", {"start": v(-372.12, -217.84) * mm, "mid": v(-373.85, -214.95) * mm, "end": v(-377.02, -213.82) * mm});
            skPoint(sketch, "E365.visualSharp", {"position": v(-357.92, -288.82) * mm});
            skArc(sketch, "E365.filletArc", {"start": v(-364.02, -288.82) * mm, "mid": v(-360.16, -286.99) * mm, "end": v(-359.12, -282.84) * mm});
            skPoint(sketch, "E366.visualSharp", {"position": v(-437.92, -288.82) * mm});
            skArc(sketch, "E366.filletArc", {"start": v(-436.73, -282.84) * mm, "mid": v(-435.7, -286.99) * mm, "end": v(-431.82, -288.82) * mm});
            skLineSegment(sketch, "E367.bottom", {"start": v(-375.27, -268.32) * mm, "end": v(-420.27, -268.32) * mm, "construction": true});
            skLineSegment(sketch, "E367.top", {"start": v(-375.27, -223.32) * mm, "end": v(-420.27, -223.32) * mm});
            skLineSegment(sketch, "E367.left", {"start": v(-375.27, -268.32) * mm, "end": v(-375.27, -223.32) * mm, "construction": true});
            skLineSegment(sketch, "E367.right", {"start": v(-420.27, -268.32) * mm, "end": v(-420.27, -223.32) * mm, "construction": true});
            skLineSegment(sketch, "E368.bottom", {"start": v(-423.73, -217.84) * mm, "end": v(-372.12, -217.84) * mm});
            skLineSegment(sketch, "E368.top", {"start": v(-418.73, -206.66) * mm, "end": v(-377.12, -206.66) * mm});
            skLineSegment(sketch, "E368.left", {"start": v(-423.73, -217.84) * mm, "end": v(-423.73, -211.66) * mm});
            skLineSegment(sketch, "E368.right", {"start": v(-372.12, -217.84) * mm, "end": v(-372.12, -211.66) * mm});
            skLineSegment(sketch, "E369", {"start": v(-392.93, -213.82) * mm, "end": v(-392.93, -197.58) * mm, "construction": true});
            skLineSegment(sketch, "E370", {"start": v(-402.92, -213.82) * mm, "end": v(-402.92, -198.1) * mm, "construction": true});
            skCircle(sketch, "E371", {"center": v(-408.06, -213.82) * mm, "radius": 2.5 * mm});
            skCircle(sketch, "E372", {"center": v(-387.79, -213.82) * mm, "radius": 2.5 * mm});
            skCircle(sketch, "E373", {"center": v(-408.06, -213.82) * mm, "radius": 5 * mm, "construction": true});
            skCircle(sketch, "E374", {"center": v(-387.79, -213.82) * mm, "radius": 5 * mm, "construction": true});
            skPoint(sketch, "E375.visualSharp", {"position": v(-372.12, -206.66) * mm});
            skArc(sketch, "E375.filletArc", {"start": v(-372.12, -211.66) * mm, "mid": v(-373.58, -208.12) * mm, "end": v(-377.12, -206.66) * mm});
            skPoint(sketch, "E376.visualSharp", {"position": v(-423.73, -206.66) * mm});
            skArc(sketch, "E376.filletArc", {"start": v(-418.73, -206.66) * mm, "mid": v(-422.26, -208.12) * mm, "end": v(-423.73, -211.66) * mm});
            skSolve(sketch);
        }
        {
            var Q0;
            Q0=makeQuery(id+"F11.opExtrude","SWEPT_FACE",FACE,{"disambiguationData":[OSD([sQuery(id+"F10.wireOp",EDGE,"E317.top"),sQuery(id+"F10.wireOp",EDGE,"E319.bottom"),sQuery(id+"F10.wireOp",EDGE,"E320.top")])]});
            var sketch = newSketch(context, id + "F28", { "sketchPlane" : qUnion([Q0])});
            skLineSegment(sketch, "E377.bottom", {"start": v(-360.66, 8.18) * mm, "end": v(-310.66, 8.18) * mm});
            skLineSegment(sketch, "E377.top", {"start": v(-360.66, 3.17) * mm, "end": v(-310.66, 3.17) * mm});
            skLineSegment(sketch, "E377.left", {"start": v(-360.66, 8.18) * mm, "end": v(-360.66, 3.17) * mm});
            skLineSegment(sketch, "E377.right", {"start": v(-310.66, 8.18) * mm, "end": v(-310.66, 3.17) * mm});
            skLineSegment(sketch, "E378.top", {"start": v(-360.66, -36.32) * mm, "end": v(-310.66, -36.32) * mm});
            skLineSegment(sketch, "E378.left", {"start": v(-360.66, 3.18) * mm, "end": v(-360.66, -36.32) * mm});
            skLineSegment(sketch, "E378.right", {"start": v(-310.66, 3.18) * mm, "end": v(-310.66, -36.32) * mm});
            skLineSegment(sketch, "E379.top", {"start": v(-360.66, -11.32) * mm, "end": v(-310.66, -11.32) * mm});
            skLineSegment(sketch, "E379.left", {"start": v(-360.66, -36.32) * mm, "end": v(-360.66, -11.33) * mm});
            skLineSegment(sketch, "E379.right", {"start": v(-310.66, -36.32) * mm, "end": v(-310.66, -11.33) * mm});
            skLineSegment(sketch, "E380.bottom", {"start": v(-322.66, 8.18) * mm, "end": v(-348.66, 8.18) * mm});
            skLineSegment(sketch, "E380.top", {"start": v(-322.66, -36.32) * mm, "end": v(-348.66, -36.33) * mm});
            skLineSegment(sketch, "E380.left", {"start": v(-322.66, 8.18) * mm, "end": v(-322.66, -36.32) * mm});
            skLineSegment(sketch, "E380.right", {"start": v(-348.66, 8.18) * mm, "end": v(-348.66, -36.32) * mm});
            skLineSegment(sketch, "E381", {"start": v(-322.66, -36.33) * mm, "end": v(-310.66, 3.17) * mm});
            skCircle(sketch, "E382", {"center": v(-326.16, -42.33) * mm, "radius": 1.5 * mm});
            skCircle(sketch, "E383", {"center": v(-331.16, -35.32) * mm, "radius": 1.5 * mm});
            skCircle(sketch, "E384", {"center": v(-331.16, -42.33) * mm, "radius": 1.5 * mm});
            skCircle(sketch, "E385", {"center": v(-326.16, -35.32) * mm, "radius": 1.5 * mm});
            skLineSegment(sketch, "E386", {"start": v(-326.16, -42.33) * mm, "end": v(-331.16, -35.32) * mm, "construction": true});
            skLineSegment(sketch, "E387", {"start": v(-331.16, -42.33) * mm, "end": v(-326.16, -35.32) * mm, "construction": true});
            skPoint(sketch, "E388", {"position": v(-328.66, -38.82) * mm});
            skCircle(sketch, "E389", {"center": v(-340.16, -42.33) * mm, "radius": 1.5 * mm});
            skCircle(sketch, "E390", {"center": v(-345.16, -35.32) * mm, "radius": 1.5 * mm});
            skCircle(sketch, "E391", {"center": v(-345.16, -42.33) * mm, "radius": 1.5 * mm});
            skCircle(sketch, "E392", {"center": v(-340.16, -35.32) * mm, "radius": 1.5 * mm});
            skLineSegment(sketch, "E393", {"start": v(-340.16, -42.33) * mm, "end": v(-345.16, -35.32) * mm, "construction": true});
            skLineSegment(sketch, "E394", {"start": v(-345.16, -42.33) * mm, "end": v(-340.16, -35.32) * mm, "construction": true});
            skPoint(sketch, "E395", {"position": v(-342.66, -38.82) * mm});
            skPoint(sketch, "E396", {"position": v(-360.66, -23.83) * mm});
            skLineSegment(sketch, "E397.bottom", {"start": v(-295.1, -33.82) * mm, "end": v(-285.1, -33.82) * mm});
            skLineSegment(sketch, "E397.top", {"start": v(-295.1, -13.82) * mm, "end": v(-285.1, -13.82) * mm});
            skLineSegment(sketch, "E397.left", {"start": v(-295.1, -33.82) * mm, "end": v(-295.1, -13.82) * mm});
            skLineSegment(sketch, "E397.right", {"start": v(-285.1, -33.82) * mm, "end": v(-285.1, -13.82) * mm});
            skCircle(sketch, "E398", {"center": v(-290.1, -23.82) * mm, "radius": 2.65 * mm});
            skPoint(sketch, "E399", {"position": v(-295.1, -23.82) * mm});
            skPoint(sketch, "E400", {"position": v(-290.1, -13.82) * mm});
            skLineSegment(sketch, "E401.left", {"start": v(-322.66, -17.32) * mm, "end": v(-322.66, -30.32) * mm});
            skLineSegment(sketch, "E402.bottom", {"start": v(-348.66, -36.33) * mm, "end": v(-322.66, -36.33) * mm});
            skLineSegment(sketch, "E402.top", {"start": v(-348.66, -47.12) * mm, "end": v(-322.66, -47.12) * mm});
            skLineSegment(sketch, "E402.left", {"start": v(-348.66, -36.33) * mm, "end": v(-348.66, -47.12) * mm});
            skLineSegment(sketch, "E402.right", {"start": v(-322.66, -36.33) * mm, "end": v(-322.66, -47.12) * mm});
            skLineSegment(sketch, "E403.bottom", {"start": v(-322.66, -47.12) * mm, "end": v(-348.66, -47.12) * mm});
            skLineSegment(sketch, "E403.top", {"start": v(-322.66, -51.12) * mm, "end": v(-348.66, -51.12) * mm});
            skLineSegment(sketch, "E403.left", {"start": v(-322.66, -47.12) * mm, "end": v(-322.66, -51.12) * mm});
            skLineSegment(sketch, "E403.right", {"start": v(-348.66, -47.12) * mm, "end": v(-348.66, -51.12) * mm});
            skLineSegment(sketch, "E404", {"start": v(-348.66, -36.32) * mm, "end": v(-360.66, 3.17) * mm});
            skSolve(sketch);
        }
        {
            var Q0;
            {var subQ0=sQuery(id+"F28.wireOp",EDGE,"E380.left");var subQ1=sQuery(id+"F28.wireOp",EDGE,"E377.bottom");var subQ2=makeQuery(id+"F28.imprint","INTERSECT",VERTEX,{"derivedFrom":[subQ1,subQ0]});Q0=makeQuery(id+"F28.imprint","IMPRINT",FACE,{"disambiguationData":[TD([[makeQuery(id+"F28.imprint","IMPRINT",EDGE,{"disambiguationData":[TD([[subQ2,-1.0]])],"derivedFrom":subQ1}),1.0]])]});}
            var Q1;
            {var subQ0=sQuery(id+"F28.wireOp",EDGE,"E380.left");var subQ1=sQuery(id+"F28.wireOp",EDGE,"E377.top");var subQ2=makeQuery(id+"F28.imprint","INTERSECT",VERTEX,{"derivedFrom":[subQ1,subQ0]});Q1=makeQuery(id+"F28.imprint","IMPRINT",FACE,{"disambiguationData":[TD([[makeQuery(id+"F28.imprint","IMPRINT",EDGE,{"disambiguationData":[TD([[subQ2,-1.0]])],"derivedFrom":subQ1}),1.0]])]});}
            var Q2;
            {var subQ0=sQuery(id+"F28.wireOp",EDGE,"E377.right");Q2=makeQuery(id+"F28.imprint","IMPRINT",FACE,{"disambiguationData":[TD([[makeQuery(id+"F28.imprint","IMPRINT",EDGE,{"derivedFrom":subQ0}),-1.0]])]});}
            var Q3;
            {var subQ3=sQuery(id+"F28.wireOp",EDGE,"E380.right");var subQ5=sQuery(id+"F28.wireOp",EDGE,"E377.top");var subQ6=makeQuery(id+"F28.imprint","INTERSECT",VERTEX,{"derivedFrom":[subQ5,subQ3]});Q3=makeQuery(id+"F28.imprint","IMPRINT",FACE,{"disambiguationData":[TD([[makeQuery(id+"F28.imprint","IMPRINT",EDGE,{"disambiguationData":[TD([[subQ6,-1.0]])],"derivedFrom":subQ5}),-1.0]])]});}
            var Q4;
            Q4=makeQuery(id+"F28.imprint","IMPRINT",FACE,{"disambiguationData":[TD([[makeQuery(id+"F28.imprint","IMPRINT",EDGE,{"derivedFrom":sQuery(id+"F28.wireOp",EDGE,"A7xuxMXy-dTGL-ZxwL-iAK5-ICeju24WDyET")}),-1.0]])]});
            var Q5;
            Q5=makeQuery(id+"F28.imprint","IMPRINT",FACE,{"disambiguationData":[TD([[makeQuery(id+"F28.imprint","IMPRINT",EDGE,{"derivedFrom":sQuery(id+"F28.wireOp",EDGE,"E382")}),-1.0]])]});
            var Q6;
            {var subQ0=sQuery(id+"F28.wireOp",EDGE,"E381");var subQ1=sQuery(id+"F28.wireOp",EDGE,"E379.top");var subQ2=makeQuery(id+"F28.imprint","INTERSECT",VERTEX,{"derivedFrom":[subQ1,subQ0]});Q6=makeQuery(id+"F28.imprint","IMPRINT",FACE,{"disambiguationData":[TD([[makeQuery(id+"F28.imprint","IMPRINT",EDGE,{"disambiguationData":[TD([[subQ2,1.0]])],"derivedFrom":subQ1}),-1.0]])]});}
            var Q7;
            {var subQ0=sQuery(id+"F28.wireOp",EDGE,"E380.right");var subQ1=sQuery(id+"F28.wireOp",EDGE,"E379.top");var subQ2=makeQuery(id+"F28.imprint","INTERSECT",VERTEX,{"derivedFrom":[subQ1,subQ0]});Q7=makeQuery(id+"F28.imprint","IMPRINT",FACE,{"disambiguationData":[TD([[makeQuery(id+"F28.imprint","IMPRINT",EDGE,{"disambiguationData":[TD([[subQ2,1.0]])],"derivedFrom":subQ1}),-1.0]])]});}
            var Q8;
            {var subQ0=sQuery(id+"F28.wireOp",EDGE,"E380.right");var subQ1=sQuery(id+"F28.wireOp",EDGE,"E377.top");var subQ2=makeQuery(id+"F28.imprint","INTERSECT",VERTEX,{"derivedFrom":[subQ1,subQ0]});Q8=makeQuery(id+"F28.imprint","IMPRINT",FACE,{"disambiguationData":[TD([[makeQuery(id+"F28.imprint","IMPRINT",EDGE,{"disambiguationData":[TD([[subQ2,-1.0]])],"derivedFrom":subQ1}),1.0]])]});}
            var Q9;
            {var subQ0=sQuery(id+"F28.wireOp",EDGE,"E381");var subQ5=sQuery(id+"F28.wireOp",EDGE,"E379.top");var subQ6=makeQuery(id+"F28.imprint","INTERSECT",VERTEX,{"derivedFrom":[subQ5,subQ0]});Q9=makeQuery(id+"F28.imprint","IMPRINT",FACE,{"disambiguationData":[TD([[makeQuery(id+"F28.imprint","IMPRINT",EDGE,{"disambiguationData":[TD([[subQ6,1.0]])],"derivedFrom":subQ5}),1.0]])]});}
            var Q10;
            {var subQ6=sQuery(id+"F28.wireOp",EDGE,"E401.bottom");var subQ7=sQuery(id+"F28.wireOp",EDGE,"E380.left");var subQ8=makeQuery(id+"F28.imprint","INTERSECT",VERTEX,{"derivedFrom":[subQ7,subQ6]});Q10=makeQuery(id+"F28.imprint","IMPRINT",FACE,{"disambiguationData":[TD([[makeQuery(id+"F28.imprint","IMPRINT",EDGE,{"disambiguationData":[TD([[subQ8,-1.0]])],"derivedFrom":subQ7}),1.0]])]});}
            var Q11;
            Q11=makeQuery(id+"F28.imprint","IMPRINT",FACE,{"disambiguationData":[TD([[makeQuery(id+"F28.imprint","IMPRINT",EDGE,{"derivedFrom":sQuery(id+"F28.wireOp",EDGE,"8VnAJBgw-QefC-1xRa-cyaI-NVAn6xrN9P8G")}),-1.0]])]});
            var Q12;
            Q12=makeQuery(id+"F28.imprint","IMPRINT",FACE,{"disambiguationData":[TD([[makeQuery(id+"F28.imprint","IMPRINT",EDGE,{"derivedFrom":sQuery(id+"F28.wireOp",EDGE,"E383")}),-1.0]])]});
            var Q13;
            Q13=makeQuery(id+"F28.imprint","IMPRINT",FACE,{"disambiguationData":[TD([[makeQuery(id+"F28.imprint","IMPRINT",EDGE,{"derivedFrom":sQuery(id+"F28.wireOp",EDGE,"E402.top")}),-1.0]])]});
            extrude(context, id + "F29", {"entities" : qUnion([Q0, Q1, Q2, Q3, Q4, Q5, Q6, Q7, Q8, Q9, Q10, Q11, Q12, Q13]), "depth" : 4 * mm, "offsetDistance" : 25 * mm});
        }
        {
            var Q0;
            Q0=makeQuery(id+"F29.opExtrude","CAP_FACE",FACE,{"disambiguationData":[OSD([sQuery(id+"F28.wireOp",EDGE,"E377.bottom"),sQuery(id+"F28.wireOp",EDGE,"E377.top"),sQuery(id+"F28.wireOp",EDGE,"E377.left"),sQuery(id+"F28.wireOp",EDGE,"E377.right"),sQuery(id+"F28.wireOp",EDGE,"E378.top"),sQuery(id+"F28.wireOp",EDGE,"E380.left"),sQuery(id+"F28.wireOp",EDGE,"E380.right"),sQuery(id+"F28.wireOp",EDGE,"A7xuxMXy-dTGL-ZxwL-iAK5-ICeju24WDyET"),sQuery(id+"F28.wireOp",EDGE,"fi8BFFNk-4Vmm-BGuc-pvFc-LouNcLyW44mW"),sQuery(id+"F28.wireOp",EDGE,"hp92n9pO-ApwR-SwJL-5D8E-VHKnq0ExEAzZ"),sQuery(id+"F28.wireOp",EDGE,"IFGCCrvU-3XWE-eVdl-zL66-rHxVFCVm0MUW")])],"isStart":false});
            var sketch = newSketch(context, id + "F30", { "sketchPlane" : qUnion([Q0])});
            skCircle(sketch, "E405", {"center": v(-332.16, 5.68) * mm, "radius": 1.59 * mm});
            skCircle(sketch, "E406", {"center": v(-339.16, 5.68) * mm, "radius": 1.59 * mm});
            skCircle(sketch, "E407", {"center": v(-351.16, 5.68) * mm, "radius": 1.59 * mm});
            skCircle(sketch, "E408", {"center": v(-320.16, 5.68) * mm, "radius": 1.59 * mm});
            skPoint(sketch, "E409", {"position": v(-360.66, 5.67) * mm});
            skPoint(sketch, "E410", {"position": v(-335.66, 8.18) * mm});
            skSolve(sketch);
        }
        {
            var Q0;
            Q0 = qSketchRegion(id + "F30", true);
            extrude(context, id + "F31", {"entities" : qUnion([Q0]), "operationType" : NewBodyOperationType.REMOVE, "oppositeDirection" : true, "depth" : 4 * mm, "offsetDistance" : 25 * mm});
        }
        {
            var Q0;
            Q0=makeQuery(id+"F29.opExtrude","CAP_FACE",FACE,{"disambiguationData":[OSD([sQuery(id+"F28.wireOp",EDGE,"E377.bottom"),sQuery(id+"F28.wireOp",EDGE,"E377.top"),sQuery(id+"F28.wireOp",EDGE,"E377.left"),sQuery(id+"F28.wireOp",EDGE,"E377.right"),sQuery(id+"F28.wireOp",EDGE,"E378.top"),sQuery(id+"F28.wireOp",EDGE,"E380.left"),sQuery(id+"F28.wireOp",EDGE,"E380.right"),sQuery(id+"F28.wireOp",EDGE,"A7xuxMXy-dTGL-ZxwL-iAK5-ICeju24WDyET"),sQuery(id+"F28.wireOp",EDGE,"fi8BFFNk-4Vmm-BGuc-pvFc-LouNcLyW44mW"),sQuery(id+"F28.wireOp",EDGE,"hp92n9pO-ApwR-SwJL-5D8E-VHKnq0ExEAzZ"),sQuery(id+"F28.wireOp",EDGE,"IFGCCrvU-3XWE-eVdl-zL66-rHxVFCVm0MUW")])],"isStart":false});
            var sketch = newSketch(context, id + "F32", { "sketchPlane" : qUnion([Q0])});
            skCircle(sketch, "E411", {"center": v(-320.16, 5.68) * mm, "radius": 1.4 * mm});
            skCircle(sketch, "E412", {"center": v(-332.16, 5.68) * mm, "radius": 1.4 * mm});
            skCircle(sketch, "E413", {"center": v(-339.16, 5.68) * mm, "radius": 1.4 * mm});
            skCircle(sketch, "E414", {"center": v(-351.16, 5.68) * mm, "radius": 1.4 * mm});
            skSolve(sketch);
        }
        {
            var Q0;
            Q0 = qSketchRegion(id + "F32", true);
            extrude(context, id + "F33", {"entities" : qUnion([Q0]), "operationType" : NewBodyOperationType.REMOVE, "oppositeDirection" : true, "depth" : 60 * mm, "offsetDistance" : 25 * mm});
        }
        {
            var Q0;
            Q0=makeQuery(id+"F17.opExtrude","CAP_FACE",FACE,{"disambiguationData":[OSD([sQuery(id+"F10.wireOp",EDGE,"E317.right"),sQuery(id+"F12.wireOp",EDGE,"E321.right")])],"isStart":false});
            var sketch = newSketch(context, id + "F34", { "sketchPlane" : qUnion([Q0])});
            skPoint(sketch, "E415", {"position": v(10.56, 8.18) * mm});
            skPoint(sketch, "E416", {"position": v(10.56, 53.17) * mm});
            skPoint(sketch, "E417", {"position": v(-9.6, 8.18) * mm});
            skLineSegment(sketch, "E418", {"start": v(10.56, 53.17) * mm, "end": v(-9.6, 8.18) * mm});
            skSolve(sketch);
        }
        {
            var Q0;
            Q0=qCreatedBy(makeId("Front.planeOp"),FACE);
            var sketch = newSketch(context, id + "F35", { "sketchPlane" : qUnion([Q0])});
            skLineSegment(sketch, "E419.bottom", {"start": v(-241.22, 125.01) * mm, "end": v(-189.54, 125.01) * mm});
            skLineSegment(sketch, "E419.top", {"start": v(-241.22, 105.01) * mm, "end": v(-189.54, 105.01) * mm});
            skLineSegment(sketch, "E419.right", {"start": v(-189.54, 125.01) * mm, "end": v(-189.54, 105.01) * mm});
            skLineSegment(sketch, "E420.top", {"start": v(-241.22, 52.01) * mm, "end": v(-189.54, 52.01) * mm});
            skLineSegment(sketch, "E420.left", {"start": v(-241.22, 105.01) * mm, "end": v(-241.22, 52.01) * mm});
            skLineSegment(sketch, "E420.right", {"start": v(-189.54, 105.01) * mm, "end": v(-189.54, 52.01) * mm});
            skLineSegment(sketch, "E421.top", {"start": v(-241.22, 77.01) * mm, "end": v(-189.54, 77.01) * mm});
            skLineSegment(sketch, "E421.left", {"start": v(-241.22, 52.01) * mm, "end": v(-241.22, 77.01) * mm});
            skLineSegment(sketch, "E421.right", {"start": v(-189.54, 52.01) * mm, "end": v(-189.54, 77.01) * mm});
            skLineSegment(sketch, "E422.top", {"start": v(-201.54, 52.01) * mm, "end": v(-229.22, 52.01) * mm});
            skLineSegment(sketch, "E423", {"start": v(-201.54, 52.01) * mm, "end": v(-189.54, 105.01) * mm});
            skCircle(sketch, "E424", {"center": v(-206.72, 61.01) * mm, "radius": 1.5 * mm});
            skCircle(sketch, "E425", {"center": v(-211.72, 68.01) * mm, "radius": 1.5 * mm});
            skCircle(sketch, "E426", {"center": v(-211.72, 61.01) * mm, "radius": 1.5 * mm});
            skCircle(sketch, "E427", {"center": v(-206.72, 68.01) * mm, "radius": 1.5 * mm});
            skLineSegment(sketch, "E428", {"start": v(-206.72, 61.01) * mm, "end": v(-211.72, 68.01) * mm, "construction": true});
            skLineSegment(sketch, "E429", {"start": v(-211.72, 61.01) * mm, "end": v(-206.72, 68.01) * mm, "construction": true});
            skPoint(sketch, "E430", {"position": v(-209.22, 64.51) * mm});
            skLineSegment(sketch, "E431", {"start": v(-229.22, 52.01) * mm, "end": v(-241.22, 105.01) * mm});
            skLineSegment(sketch, "E432.left", {"start": v(-241.22, 105.01) * mm, "end": v(-241.22, 125.01) * mm});
            skLineSegment(sketch, "E432.right", {"start": v(-189.54, 105.01) * mm, "end": v(-189.54, 125.01) * mm});
            skCircle(sketch, "E433", {"center": v(-226.22, 115.01) * mm, "radius": 2.65 * mm});
            skCircle(sketch, "E434", {"center": v(-204.54, 115.01) * mm, "radius": 2.65 * mm});
            skPoint(sketch, "E435", {"position": v(-189.54, 115.01) * mm});
            skSolve(sketch);
        }
        {
            var Q0;
            Q0=makeQuery(id+"F35.imprint","IMPRINT",FACE,{"disambiguationData":[TD([[makeQuery(id+"F35.imprint","IMPRINT",EDGE,{"derivedFrom":sQuery(id+"F35.wireOp",EDGE,"E419.bottom")}),-1.0]])]});
            var Q1;
            {var subQ0=sQuery(id+"F35.wireOp",EDGE,"E419.top");Q1=makeQuery(id+"F35.imprint","IMPRINT",FACE,{"disambiguationData":[TD([[makeQuery(id+"F35.imprint","IMPRINT",EDGE,{"derivedFrom":subQ0}),-1.0]])]});}
            var Q2;
            Q2=makeQuery(id+"F35.imprint","IMPRINT",FACE,{"disambiguationData":[TD([[makeQuery(id+"F35.imprint","IMPRINT",EDGE,{"derivedFrom":sQuery(id+"F35.wireOp",EDGE,"E424")}),-1.0]])]});
            extrude(context, id + "F36", {"entities" : qUnion([Q0, Q1, Q2]), "depth" : 4 * mm, "offsetDistance" : 25 * mm});
        }
        {
            var Q0;
            Q0=makeQuery(id+"F28.imprint","IMPRINT",FACE,{"disambiguationData":[TD([[makeQuery(id+"F28.imprint","IMPRINT",EDGE,{"derivedFrom":sQuery(id+"F28.wireOp",EDGE,"E397.bottom")}),1.0]])]});
            extrude(context, id + "F37", {"entities" : qUnion([Q0]), "depth" : 9 * mm, "offsetDistance" : 25 * mm});
        }
        {
            var Q0;
            Q0=makeQuery(id+"F34.imprint","IMPRINT",FACE,{"disambiguationData":[TD([[makeQuery(id+"F34.imprint","IMPRINT",EDGE,{"derivedFrom":sQuery(id+"F34.wireOp",EDGE,"E418")}),1.0]])]});
            var Q1;
            {var subQ0=sQuery(id+"F12.wireOp",EDGE,"E321.right");Q1=makeQuery(id+"F34.imprint","IMPRINT",FACE,{"disambiguationData":[TD([[makeQuery(id+"F34.imprint","IMPRINT",EDGE,{"derivedFrom":makeQuery(id+"F17.opExtrude","CAP_EDGE",EDGE,{"disambiguationData":[OSD([subQ0])],"isStart":false})}),-1.0]])]});}
            extrude(context, id + "F38", {"entities" : qUnion([Q0, Q1]), "operationType" : NewBodyOperationType.ADD, "depth" : 3 * mm, "offsetDistance" : 25 * mm});
        }
        {
            var Q0;
            {var subQ0=sQuery(id+"F12.wireOp",EDGE,"E321.left");Q0=makeQuery(id+"F23.imprint","IMPRINT",FACE,{"disambiguationData":[TD([[makeQuery(id+"F23.imprint","IMPRINT",EDGE,{"derivedFrom":makeQuery(id+"F16.opExtrude","CAP_EDGE",EDGE,{"disambiguationData":[OSD([subQ0])],"isStart":false})}),1.0]])]});}
            extrude(context, id + "F39", {"entities" : qUnion([Q0]), "operationType" : NewBodyOperationType.ADD, "depth" : 3 * mm, "offsetDistance" : 25 * mm});
        }
        {
            var Q0;
            Q0=makeQuery(id+"F39.boolean.opBoolean","MERGE",FACE,{"derivedFrom":[makeQuery(id+"F11.opExtrude","SWEPT_FACE",FACE,{"disambiguationData":[OSD([sQuery(id+"F10.wireOp",EDGE,"E319.right")])]}),makeQuery(id+"F39.opExtrude","CAP_FACE",FACE,{"disambiguationData":[OSD([sQuery(id+"F10.wireOp",EDGE,"E317.left"),sQuery(id+"F10.wireOp",EDGE,"E318.bottom"),sQuery(id+"F12.wireOp",EDGE,"E321.bottom"),sQuery(id+"F12.wireOp",EDGE,"E321.top"),sQuery(id+"F12.wireOp",EDGE,"E321.left")])],"isStart":false})]});
            var sketch = newSketch(context, id + "F40", { "sketchPlane" : qUnion([Q0])});
            skLineSegment(sketch, "E436", {"start": v(-10.56, 53.17) * mm, "end": v(17.44, 8.18) * mm});
            skSolve(sketch);
        }
        {
            var Q0;
            Q0 = qSketchRegion(id + "F40", true);
            var Q1;
            Q1=makeQuery(id+"F40.imprint","IMPRINT",FACE,{"disambiguationData":[TD([[makeQuery(id+"F40.imprint","IMPRINT",EDGE,{"derivedFrom":sQuery(id+"F40.wireOp",EDGE,"E436")}),-1.0]])]});
            extrude(context, id + "F41", {"entities" : qUnion([Q0, Q1]), "operationType" : NewBodyOperationType.ADD, "oppositeDirection" : true, "depth" : 3 * mm, "offsetDistance" : 25 * mm});
        }
        {
            var Q0;
            Q0=makeQuery(id+"F38.boolean.opBoolean","MERGE",FACE,{"derivedFrom":[makeQuery(id+"F11.opExtrude","SWEPT_FACE",FACE,{"disambiguationData":[OSD([sQuery(id+"F10.wireOp",EDGE,"E320.right")])]}),makeQuery(id+"F38.opExtrude","CAP_FACE",FACE,{"disambiguationData":[OSD([sQuery(id+"F10.wireOp",EDGE,"E317.right"),sQuery(id+"F10.wireOp",EDGE,"E320.bottom"),sQuery(id+"F12.wireOp",EDGE,"E321.top"),sQuery(id+"F12.wireOp",EDGE,"E321.right"),sQuery(id+"F34.wireOp",EDGE,"E418")])],"isStart":false})]});
            var sketch = newSketch(context, id + "F42", { "sketchPlane" : qUnion([Q0])});
            skLineSegment(sketch, "E437", {"start": v(10.56, 53.17) * mm, "end": v(-17.44, 8.18) * mm});
            skSolve(sketch);
        }
        {
            var Q0;
            Q0 = qSketchRegion(id + "F42", true);
            var Q1;
            Q1=makeQuery(id+"F42.imprint","IMPRINT",FACE,{"disambiguationData":[TD([[makeQuery(id+"F42.imprint","IMPRINT",EDGE,{"derivedFrom":sQuery(id+"F42.wireOp",EDGE,"E437")}),1.0]])]});
            extrude(context, id + "F43", {"entities" : qUnion([Q0, Q1]), "operationType" : NewBodyOperationType.ADD, "oppositeDirection" : true, "depth" : 3 * mm, "offsetDistance" : 25 * mm});
        }
        {
            var Q0;
            {var subQ0=sQuery(id+"F12.wireOp",EDGE,"E321.left");var subQ1=sQuery(id+"F12.wireOp",EDGE,"E321.top");var subQ2=sQuery(id+"F12.wireOp",EDGE,"E321.right");Q0=makeQuery(id+"F39.boolean.opBoolean","MERGE",FACE,{"derivedFrom":[makeQuery(id+"F38.boolean.opBoolean","MERGE",FACE,{"derivedFrom":[makeQuery(id+"F17.boolean.opBoolean","MERGE",FACE,{"derivedFrom":[makeQuery(id+"F16.boolean.opBoolean","MERGE",FACE,{"derivedFrom":[makeQuery(id+"F14.boolean.opBoolean","MERGE",FACE,{"derivedFrom":[makeQuery(id+"F13.opExtrude","SWEPT_FACE",FACE,{"disambiguationData":[OSD([subQ1])]}),makeQuery(id+"F14.opExtrude","SWEPT_FACE",FACE,{"disambiguationData":[OSD([subQ1])]})]}),makeQuery(id+"F16.opExtrude","SWEPT_FACE",FACE,{"disambiguationData":[OSD([subQ1,subQ0])]})]}),makeQuery(id+"F17.opExtrude","SWEPT_FACE",FACE,{"disambiguationData":[OSD([subQ1,subQ2])]})]}),makeQuery(id+"F38.opExtrude","SWEPT_FACE",FACE,{"disambiguationData":[OSD([subQ1,subQ2])]})]}),makeQuery(id+"F39.opExtrude","SWEPT_FACE",FACE,{"disambiguationData":[OSD([subQ1,subQ0])]})]});}
            extrude(context, id + "F44", {"entities" : qUnion([Q0]), "operationType" : NewBodyOperationType.ADD, "depth" : 2.5 * mm, "offsetDistance" : 25 * mm});
        }
        {
            var Q0;
            Q0=qCreatedBy(makeId("Top.planeOp"),FACE);
            var sketch = newSketch(context, id + "F45", { "sketchPlane" : qUnion([Q0])});
            skCircle(sketch, "E438", {"center": v(-206.32, 28.42) * mm, "radius": 2.75 * mm});
            skSolve(sketch);
        }
        {
            var Q0;
            Q0 = qSketchRegion(id + "F45", true);
            var Q1;
            Q1=makeQuery(id+"F45.imprint","IMPRINT",FACE,{"disambiguationData":[TD([[makeQuery(id+"F45.imprint","IMPRINT",EDGE,{"derivedFrom":sQuery(id+"F45.wireOp",EDGE,"E438")}),1.0]])]});
            extrude(context, id + "F46", {"entities" : qUnion([Q0, Q1]), "depth" : 4 * mm, "offsetDistance" : 25 * mm});
        }
        {
            var Q0;
            Q0=makeQuery(id+"F46.opExtrude","CAP_FACE",FACE,{"disambiguationData":[OSD([sQuery(id+"F45.wireOp",EDGE,"E438")])],"isStart":true});
            var sketch = newSketch(context, id + "F47", { "sketchPlane" : qUnion([Q0])});
            skCircle(sketch, "E439", {"center": v(-206.32, -28.42) * mm, "radius": 4.5 * mm});
            skSolve(sketch);
        }
        {
            var Q0;
            Q0 = qSketchRegion(id + "F47", true);
            extrude(context, id + "F48", {"entities" : qUnion([Q0]), "operationType" : NewBodyOperationType.ADD, "depth" : 2 * mm, "offsetDistance" : 25 * mm});
        }
        {
            var Q0;
            Q0=makeQuery(id+"F48.opExtrude","CAP_FACE",FACE,{"disambiguationData":[OSD([sQuery(id+"F47.wireOp",EDGE,"E439")])],"isStart":false});
            var sketch = newSketch(context, id + "F49", { "sketchPlane" : qUnion([Q0])});
            skCircle(sketch, "E440", {"center": v(-206.32, -28.42) * mm, "radius": 2.5 * mm});
            skSolve(sketch);
        }
        {
            var Q0;
            Q0=makeQuery(id+"F49.imprint","IMPRINT",FACE,{"disambiguationData":[TD([[makeQuery(id+"F49.imprint","IMPRINT",EDGE,{"derivedFrom":sQuery(id+"F49.wireOp",EDGE,"E440")}),1.0]])]});
            extrude(context, id + "F50", {"entities" : qUnion([Q0]), "operationType" : NewBodyOperationType.ADD, "depth" : 4 * mm, "offsetDistance" : 25 * mm});
        }
        {
            var Q0;
            Q0=makeQuery(id+"F28.imprint","IMPRINT",FACE,{"disambiguationData":[TD([[makeQuery(id+"F28.imprint","IMPRINT",EDGE,{"derivedFrom":sQuery(id+"F28.wireOp",EDGE,"E402.top")}),-1.0]])]});
            extrude(context, id + "F51", {"entities" : qUnion([Q0]), "operationType" : NewBodyOperationType.ADD, "oppositeDirection" : true, "depth" : 36.68 * mm, "offsetDistance" : 25 * mm});
        }
        {
            var Q0;
            Q0=makeQuery(id+"F44.opExtrude","CAP_FACE",FACE,{"disambiguationData":[OSD([sQuery(id+"F12.wireOp",EDGE,"E321.top"),sQuery(id+"F12.wireOp",EDGE,"E321.left"),sQuery(id+"F12.wireOp",EDGE,"E321.right")])],"isStart":false});
            var sketch = newSketch(context, id + "F52", { "sketchPlane" : qUnion([Q0])});
            skLineSegment(sketch, "E441.bottom", {"start": v(360.66, 3.17) * mm, "end": v(310.66, 3.17) * mm});
            skLineSegment(sketch, "E441.top", {"start": v(360.66, 8.18) * mm, "end": v(310.66, 8.17) * mm});
            skLineSegment(sketch, "E441.left", {"start": v(360.66, 3.17) * mm, "end": v(360.66, 8.18) * mm});
            skLineSegment(sketch, "E441.right", {"start": v(310.66, 3.17) * mm, "end": v(310.66, 8.18) * mm});
            skLineSegment(sketch, "E442.top", {"start": v(360.66, -51.12) * mm, "end": v(310.66, -51.12) * mm});
            skLineSegment(sketch, "E442.left", {"start": v(360.66, 3.18) * mm, "end": v(360.66, -51.12) * mm});
            skLineSegment(sketch, "E442.right", {"start": v(310.66, 3.18) * mm, "end": v(310.66, -51.12) * mm});
            skPoint(sketch, "E443", {"position": v(348.5, -51.12) * mm});
            skPoint(sketch, "E444", {"position": v(322.65, -51.12) * mm});
            skPoint(sketch, "E445", {"position": v(322.66, -47.14) * mm});
            skPoint(sketch, "E446", {"position": v(348.67, -47.13) * mm});
            skLineSegment(sketch, "E447", {"start": v(348.5, -51.12) * mm, "end": v(322.65, -51.12) * mm});
            skLineSegment(sketch, "E448", {"start": v(322.66, -47.14) * mm, "end": v(310.66, 3.18) * mm});
            skLineSegment(sketch, "E449", {"start": v(360.66, 3.18) * mm, "end": v(348.67, -47.13) * mm});
            skLineSegment(sketch, "E450", {"start": v(310.66, 3.17) * mm, "end": v(360.66, 3.17) * mm});
            skLineSegment(sketch, "E451", {"start": v(348.67, -47.13) * mm, "end": v(348.5, -51.12) * mm});
            skLineSegment(sketch, "E452", {"start": v(322.65, -51.12) * mm, "end": v(322.66, -47.14) * mm});
            skSolve(sketch);
        }
        {
            var Q0;
            Q0=makeQuery(id+"F52.imprint","IMPRINT",FACE,{"disambiguationData":[TD([[makeQuery(id+"F52.imprint","IMPRINT",EDGE,{"derivedFrom":sQuery(id+"F52.wireOp",EDGE,"E441.bottom")}),-1.0]])]});
            var Q1;
            Q1=makeQuery(id+"F52.imprint","IMPRINT",FACE,{"disambiguationData":[TD([[makeQuery(id+"F52.imprint","IMPRINT",EDGE,{"derivedFrom":sQuery(id+"F52.wireOp",EDGE,"E441.bottom")}),1.0]])]});
            extrude(context, id + "F53", {"entities" : qUnion([Q0, Q1]), "operationType" : NewBodyOperationType.ADD, "depth" : 3 * mm, "offsetDistance" : 25 * mm});
        }
        {
            var Q0;
            {var subQ0=sQuery(id+"F28.wireOp",EDGE,"E403.top");Q0=makeQuery(id+"F51.boolean.opBoolean","MERGE",FACE,{"derivedFrom":[makeQuery(id+"F29.opExtrude","SWEPT_FACE",FACE,{"disambiguationData":[OSD([subQ0])]}),makeQuery(id+"F51.opExtrude","SWEPT_FACE",FACE,{"disambiguationData":[OSD([subQ0])]})]});}
            var sketch = newSketch(context, id + "F54", { "sketchPlane" : qUnion([Q0])});
            skLineSegment(sketch, "E453.bottom", {"start": v(-317.66, -19.24) * mm, "end": v(-327.66, -19.24) * mm});
            skLineSegment(sketch, "E453.top", {"start": v(-317.66, -45.24) * mm, "end": v(-327.66, -45.24) * mm});
            skLineSegment(sketch, "E453.left", {"start": v(-317.66, -19.24) * mm, "end": v(-317.66, -45.24) * mm});
            skLineSegment(sketch, "E453.right", {"start": v(-327.66, -19.24) * mm, "end": v(-327.66, -45.24) * mm});
            skLineSegment(sketch, "E454", {"start": v(-322.66, -20.63) * mm, "end": v(-322.66, -40.63) * mm, "construction": true});
            skCircle(sketch, "E455", {"center": v(-322.66, -40.63) * mm, "radius": 2.25 * mm, "construction": true});
            skPoint(sketch, "E456", {"position": v(-322.66, -19.24) * mm});
            skLineSegment(sketch, "E457.bottom", {"start": v(-327.66, -19.24) * mm, "end": v(-322.66, -19.24) * mm});
            skCircle(sketch, "E458", {"center": v(-322.66, -40.63) * mm, "radius": 2.25 * mm});
            skLineSegment(sketch, "E459", {"start": v(-327.66, -45.24) * mm, "end": v(-332.99, -19.24) * mm});
            skLineSegment(sketch, "E460", {"start": v(-332.99, -19.24) * mm, "end": v(-327.66, -19.24) * mm});
            skLineSegment(sketch, "E461", {"start": v(-317.66, -19.24) * mm, "end": v(-322.66, -13.66) * mm});
            skLineSegment(sketch, "E462", {"start": v(-322.66, -13.66) * mm, "end": v(-322.66, -19.24) * mm});
            skSolve(sketch);
        }
        {
            var Q0;
            {var subQ3=sQuery(id+"F54.wireOp",EDGE,"E457.top");Q0=makeQuery(id+"F54.imprint","IMPRINT",FACE,{"disambiguationData":[TD([[makeQuery(id+"F54.imprint","IMPRINT",EDGE,{"derivedFrom":subQ3}),1.0]])]});}
            var Q1;
            {var subQ1=sQuery(id+"F54.wireOp",EDGE,"E453.top");Q1=makeQuery(id+"F54.imprint","IMPRINT",FACE,{"disambiguationData":[TD([[makeQuery(id+"F54.imprint","IMPRINT",EDGE,{"derivedFrom":subQ1}),-1.0]])]});}
            var Q2;
            {var subQ0=sQuery(id+"F54.wireOp",EDGE,"E459");Q2=makeQuery(id+"F54.imprint","IMPRINT",FACE,{"disambiguationData":[TD([[makeQuery(id+"F54.imprint","IMPRINT",EDGE,{"derivedFrom":subQ0}),-1.0]])]});}
            extrude(context, id + "F55", {"entities" : qUnion([Q0, Q1, Q2]), "operationType" : NewBodyOperationType.ADD, "oppositeDirection" : true, "depth" : 3 * mm, "offsetDistance" : 25 * mm});
        }
        {
            var Q0;
            Q0=makeQuery(id+"F27.imprint","IMPRINT",FACE,{"disambiguationData":[TD([[makeQuery(id+"F27.imprint","IMPRINT",EDGE,{"derivedFrom":sQuery(id+"F27.wireOp",EDGE,"E343")}),-1.0]])]});
            var Q1;
            {var subQ7=sQuery(id+"F27.wireOp",EDGE,"E359");Q1=makeQuery(id+"F27.imprint","IMPRINT",FACE,{"disambiguationData":[TD([[makeQuery(id+"F27.imprint","IMPRINT",EDGE,{"derivedFrom":subQ7}),-1.0]])]});}
            var Q2;
            {var subQ4=sQuery(id+"F27.wireOp",EDGE,"E360");Q2=makeQuery(id+"F27.imprint","IMPRINT",FACE,{"disambiguationData":[TD([[makeQuery(id+"F27.imprint","IMPRINT",EDGE,{"derivedFrom":subQ4}),1.0]])]});}
            var Q3;
            Q3=makeQuery(id+"F27.imprint","IMPRINT",FACE,{"disambiguationData":[TD([[makeQuery(id+"F27.imprint","IMPRINT",EDGE,{"derivedFrom":sQuery(id+"F27.wireOp",EDGE,"E368.top")}),-1.0]])]});
            var Q4;
            {var subQ5=sQuery(id+"F27.wireOp",EDGE,"E350.top");var subQ7=sQuery(id+"F27.wireOp",EDGE,"E371");var subQ9=makeQuery(id+"F27.imprint","INTERSECT",VERTEX,{"disambiguationData":[OD(0.0)],"derivedFrom":[subQ5,subQ7]});Q4=makeQuery(id+"F27.imprint","IMPRINT",FACE,{"disambiguationData":[TD([[makeQuery(id+"F27.imprint","IMPRINT",EDGE,{"disambiguationData":[TD([[subQ9,-1.0]])],"derivedFrom":subQ5}),-1.0]])]});}
            var Q5;
            {var subQ0=sQuery(id+"F27.wireOp",EDGE,"E363.filletArc");var subQ1=sQuery(id+"F27.wireOp",EDGE,"E350.left");var subQ2=makeQuery(id+"F27.imprint","INTERSECT",VERTEX,{"derivedFrom":[subQ1,subQ0]});Q5=makeQuery(id+"F27.imprint","IMPRINT",FACE,{"disambiguationData":[TD([[makeQuery(id+"F27.imprint","IMPRINT",EDGE,{"disambiguationData":[TD([[subQ2,1.0]])],"derivedFrom":subQ1}),1.0]])]});}
            var Q6;
            {var subQ0=sQuery(id+"F27.wireOp",EDGE,"E364.filletArc");var subQ1=sQuery(id+"F27.wireOp",EDGE,"E350.right");var subQ2=makeQuery(id+"F27.imprint","INTERSECT",VERTEX,{"derivedFrom":[subQ1,subQ0]});Q6=makeQuery(id+"F27.imprint","IMPRINT",FACE,{"disambiguationData":[TD([[makeQuery(id+"F27.imprint","IMPRINT",EDGE,{"disambiguationData":[TD([[subQ2,1.0]])],"derivedFrom":subQ1}),-1.0]])]});}
            extrude(context, id + "F56", {"entities" : qUnion([Q0, Q1, Q2, Q3, Q4, Q5, Q6]), "depth" : 3.17 * mm, "offsetDistance" : 25 * mm});
        }
        {
            var Q0;
            Q0=qCreatedBy(makeId("Top.planeOp"),FACE);
            var sketch = newSketch(context, id + "F57", { "sketchPlane" : qUnion([Q0])});
            skLineSegment(sketch, "E463.bottom", {"start": v(1154.37, 294.91) * mm, "end": v(1154.37, 314.91) * mm, "construction": true});
            skLineSegment(sketch, "E463.left", {"start": v(1154.37, 294.91) * mm, "end": v(1190.37, 294.91) * mm, "construction": true});
            skCircle(sketch, "E464", {"center": v(1190.37, 336.06) * mm, "radius": 4.25 * mm});
            skLineSegment(sketch, "E465.bottom", {"start": v(1208.37, 299.91) * mm, "end": v(1208.37, 348.06) * mm});
            skLineSegment(sketch, "E465.top", {"start": v(1172.37, 299.91) * mm, "end": v(1172.37, 348.06) * mm});
            skLineSegment(sketch, "E465.left", {"start": v(1203.37, 294.91) * mm, "end": v(1177.37, 294.91) * mm});
            skLineSegment(sketch, "E465.right", {"start": v(1203.37, 353.06) * mm, "end": v(1177.37, 353.06) * mm});
            skCircle(sketch, "E466", {"center": v(1200.37, 304.91) * mm, "radius": 2.6 * mm});
            skCircle(sketch, "E467", {"center": v(1180.37, 304.91) * mm, "radius": 2.6 * mm});
            skCircle(sketch, "E468", {"center": v(1190.37, 336.06) * mm, "radius": 11 * mm});
            skPoint(sketch, "E469.visualSharp", {"position": v(1172.37, 353.06) * mm});
            skArc(sketch, "E469.filletArc", {"start": v(1177.37, 353.06) * mm, "mid": v(1173.83, 351.6) * mm, "end": v(1172.37, 348.06) * mm});
            skPoint(sketch, "E470.visualSharp", {"position": v(1208.37, 353.06) * mm});
            skArc(sketch, "E470.filletArc", {"start": v(1208.37, 348.06) * mm, "mid": v(1206.9, 351.6) * mm, "end": v(1203.37, 353.06) * mm});
            skPoint(sketch, "E471.visualSharp", {"position": v(1172.37, 294.91) * mm});
            skArc(sketch, "E471.filletArc", {"start": v(1172.37, 299.91) * mm, "mid": v(1173.83, 296.38) * mm, "end": v(1177.37, 294.91) * mm});
            skPoint(sketch, "E472.visualSharp", {"position": v(1208.37, 294.91) * mm});
            skArc(sketch, "E472.filletArc", {"start": v(1203.37, 294.91) * mm, "mid": v(1206.9, 296.38) * mm, "end": v(1208.37, 299.91) * mm});
            skCircle(sketch, "E473", {"center": v(1264.86, 315.41) * mm, "radius": 11 * mm});
            skCircle(sketch, "E474", {"center": v(1254.86, 333.29) * mm, "radius": 2.6 * mm});
            skCircle(sketch, "E475", {"center": v(1274.86, 333.29) * mm, "radius": 2.6 * mm});
            skLineSegment(sketch, "E476.bottom", {"start": v(1251.86, 298.41) * mm, "end": v(1277.86, 298.41) * mm});
            skLineSegment(sketch, "E476.top", {"start": v(1251.86, 343.29) * mm, "end": v(1277.86, 343.29) * mm});
            skLineSegment(sketch, "E476.left", {"start": v(1246.86, 303.41) * mm, "end": v(1246.86, 338.29) * mm});
            skLineSegment(sketch, "E476.right", {"start": v(1282.86, 303.41) * mm, "end": v(1282.86, 338.29) * mm});
            skPoint(sketch, "E477.visualSharp", {"position": v(1282.86, 343.29) * mm});
            skArc(sketch, "E477.filletArc", {"start": v(1282.86, 338.29) * mm, "mid": v(1281.4, 341.82) * mm, "end": v(1277.86, 343.29) * mm});
            skPoint(sketch, "E478.visualSharp", {"position": v(1246.86, 343.29) * mm});
            skArc(sketch, "E478.filletArc", {"start": v(1251.86, 343.29) * mm, "mid": v(1248.33, 341.82) * mm, "end": v(1246.86, 338.29) * mm});
            skPoint(sketch, "E479.visualSharp", {"position": v(1246.86, 298.41) * mm});
            skArc(sketch, "E479.filletArc", {"start": v(1246.86, 303.41) * mm, "mid": v(1248.33, 299.88) * mm, "end": v(1251.86, 298.41) * mm});
            skPoint(sketch, "E480.visualSharp", {"position": v(1282.86, 298.41) * mm});
            skArc(sketch, "E480.filletArc", {"start": v(1277.86, 298.41) * mm, "mid": v(1281.4, 299.88) * mm, "end": v(1282.86, 303.41) * mm});
            skPoint(sketch, "E481", {"position": v(1190.37, 353.06) * mm});
            skLineSegment(sketch, "E482", {"start": v(1190.37, 336.06) * mm, "end": v(1190.37, 294.91) * mm, "construction": true});
            skLineSegment(sketch, "E483", {"start": v(1264.86, 315.41) * mm, "end": v(1264.86, 343.29) * mm, "construction": true});
            skLineSegment(sketch, "E484", {"start": v(1172.37, 353.06) * mm, "end": v(1172.37, 294.91) * mm});
            skCircle(sketch, "E485", {"center": v(1264.86, 315.41) * mm, "radius": 4.25 * mm});
            skCircle(sketch, "E486", {"center": v(1178.87, 391.92) * mm, "radius": 4.25 * mm});
            skCircle(sketch, "E487", {"center": v(1168.87, 427.73) * mm, "radius": 2.65 * mm});
            skCircle(sketch, "E488", {"center": v(1188.87, 427.73) * mm, "radius": 2.65 * mm});
            skLineSegment(sketch, "E489.bottom", {"start": v(1160.87, 385.67) * mm, "end": v(1160.87, 432.73) * mm});
            skLineSegment(sketch, "E489.top", {"start": v(1196.87, 385.67) * mm, "end": v(1196.87, 432.73) * mm});
            skLineSegment(sketch, "E489.left", {"start": v(1165.87, 380.67) * mm, "end": v(1191.87, 380.67) * mm});
            skLineSegment(sketch, "E489.right", {"start": v(1165.87, 437.73) * mm, "end": v(1191.87, 437.73) * mm});
            skPoint(sketch, "E490.visualSharp", {"position": v(1160.87, 380.67) * mm});
            skArc(sketch, "E490.filletArc", {"start": v(1160.87, 385.67) * mm, "mid": v(1162.34, 382.14) * mm, "end": v(1165.87, 380.67) * mm});
            skPoint(sketch, "E491.visualSharp", {"position": v(1196.87, 380.67) * mm});
            skArc(sketch, "E491.filletArc", {"start": v(1191.87, 380.67) * mm, "mid": v(1195.41, 382.14) * mm, "end": v(1196.87, 385.67) * mm});
            skPoint(sketch, "E492.visualSharp", {"position": v(1196.87, 437.73) * mm});
            skArc(sketch, "E492.filletArc", {"start": v(1196.87, 432.73) * mm, "mid": v(1195.41, 436.27) * mm, "end": v(1191.87, 437.73) * mm});
            skPoint(sketch, "E493.visualSharp", {"position": v(1160.87, 437.73) * mm});
            skArc(sketch, "E493.filletArc", {"start": v(1165.87, 437.73) * mm, "mid": v(1162.34, 436.27) * mm, "end": v(1160.87, 432.73) * mm});
            skCircle(sketch, "E494", {"center": v(1178.87, 391.92) * mm, "radius": 5.25 * mm});
            skCircle(sketch, "E495", {"center": v(1173.22, 386.26) * mm, "radius": 1.65 * mm});
            skCircle(sketch, "E496", {"center": v(1173.22, 397.58) * mm, "radius": 1.65 * mm});
            skCircle(sketch, "E497", {"center": v(1184.53, 397.58) * mm, "radius": 1.65 * mm});
            skCircle(sketch, "E498", {"center": v(1184.53, 386.26) * mm, "radius": 1.65 * mm});
            skLineSegment(sketch, "E499", {"start": v(1184.53, 386.26) * mm, "end": v(1173.22, 397.58) * mm, "construction": true});
            skLineSegment(sketch, "E500", {"start": v(1173.22, 386.26) * mm, "end": v(1184.53, 397.58) * mm, "construction": true});
            skPoint(sketch, "E501", {"position": v(1178.87, 437.73) * mm});
            skPoint(sketch, "E502", {"position": v(1178.87, 380.67) * mm});
            skLineSegment(sketch, "E503.bottom", {"start": v(1233.1, 366.6) * mm, "end": v(1259.1, 366.6) * mm});
            skLineSegment(sketch, "E503.left", {"start": v(1228.1, 371.6) * mm, "end": v(1228.1, 399.19) * mm});
            skLineSegment(sketch, "E503.right", {"start": v(1264.1, 371.6) * mm, "end": v(1264.1, 399.19) * mm});
            skCircle(sketch, "E504", {"center": v(1240.43, 400.11) * mm, "radius": 1.65 * mm});
            skCircle(sketch, "E505", {"center": v(1251.75, 400.11) * mm, "radius": 1.65 * mm});
            skCircle(sketch, "E506", {"center": v(1251.75, 388.8) * mm, "radius": 1.65 * mm});
            skCircle(sketch, "E507", {"center": v(1240.43, 388.8) * mm, "radius": 1.65 * mm});
            skCircle(sketch, "E508", {"center": v(1246.1, 394.46) * mm, "radius": 3.73 * mm});
            skLineSegment(sketch, "E509.top", {"start": v(1233.1, 404.19) * mm, "end": v(1259.1, 404.19) * mm});
            skLineSegment(sketch, "E509.left", {"start": v(1221.1, 402.12) * mm, "end": v(1221.1, 404.44) * mm});
            skLineSegment(sketch, "E509.right", {"start": v(1271.1, 402.12) * mm, "end": v(1271.1, 404.44) * mm});
            skCircle(sketch, "E510", {"center": v(1236.1, 376.6) * mm, "radius": 2.65 * mm});
            skCircle(sketch, "E511", {"center": v(1256.1, 376.6) * mm, "radius": 2.65 * mm});
            skPoint(sketch, "E512.newPointA", {"position": v(1264.1, 404.19) * mm});
            skPoint(sketch, "E512.newPointB", {"position": v(1264.1, 402.14) * mm});
            skArc(sketch, "E512.filletArc", {"start": v(1264.1, 399.19) * mm, "mid": v(1262.63, 402.72) * mm, "end": v(1259.1, 404.19) * mm});
            skArc(sketch, "E513.filletArc", {"start": v(1233.1, 404.19) * mm, "mid": v(1229.56, 402.72) * mm, "end": v(1228.1, 399.19) * mm});
            skPoint(sketch, "E514.visualSharp", {"position": v(1228.1, 366.6) * mm});
            skArc(sketch, "E514.filletArc", {"start": v(1228.1, 371.6) * mm, "mid": v(1229.56, 368.06) * mm, "end": v(1233.1, 366.6) * mm});
            skPoint(sketch, "E515.visualSharp", {"position": v(1264.1, 366.6) * mm});
            skArc(sketch, "E515.filletArc", {"start": v(1259.1, 366.6) * mm, "mid": v(1262.63, 368.06) * mm, "end": v(1264.1, 371.6) * mm});
            skPoint(sketch, "E516", {"position": v(1246.1, 404.19) * mm});
            skPoint(sketch, "E517", {"position": v(1246.1, 366.6) * mm});
            skLineSegment(sketch, "E518", {"start": v(1251.75, 400.11) * mm, "end": v(1240.43, 388.8) * mm, "construction": true});
            skLineSegment(sketch, "E519", {"start": v(1240.43, 400.11) * mm, "end": v(1251.75, 388.8) * mm, "construction": true});
            skLineSegment(sketch, "E520", {"start": v(1236.1, 376.6) * mm, "end": v(1256.1, 376.6) * mm, "construction": true});
            skPoint(sketch, "E521", {"position": v(1246.1, 376.6) * mm});
            skSolve(sketch);
        }
        {
            var Q0;
            Q0=makeQuery(id+"F57.imprint","IMPRINT",FACE,{"disambiguationData":[TD([[makeQuery(id+"F57.imprint","IMPRINT",EDGE,{"derivedFrom":sQuery(id+"F57.wireOp",EDGE,"E487")}),-1.0]])]});
            var Q1;
            Q1=makeQuery(id+"F57.imprint","IMPRINT",FACE,{"disambiguationData":[TD([[makeQuery(id+"F57.imprint","IMPRINT",EDGE,{"derivedFrom":sQuery(id+"F57.wireOp",EDGE,"E503.bottom")}),1.0]])]});
            var Q2;
            Q2=makeQuery(id+"F57.imprint","IMPRINT",FACE,{"disambiguationData":[TD([[makeQuery(id+"F57.imprint","IMPRINT",EDGE,{"derivedFrom":sQuery(id+"F57.wireOp",EDGE,"E465.bottom")}),1.0]])]});
            var Q3;
            Q3=makeQuery(id+"F57.imprint","IMPRINT",FACE,{"disambiguationData":[TD([[makeQuery(id+"F57.imprint","IMPRINT",EDGE,{"derivedFrom":sQuery(id+"F57.wireOp",EDGE,"E473")}),-1.0]])]});
            extrude(context, id + "F58", {"entities" : qUnion([Q0, Q1, Q2, Q3]), "depth" : 3.17 * mm, "offsetDistance" : 25 * mm});
        }
    });
